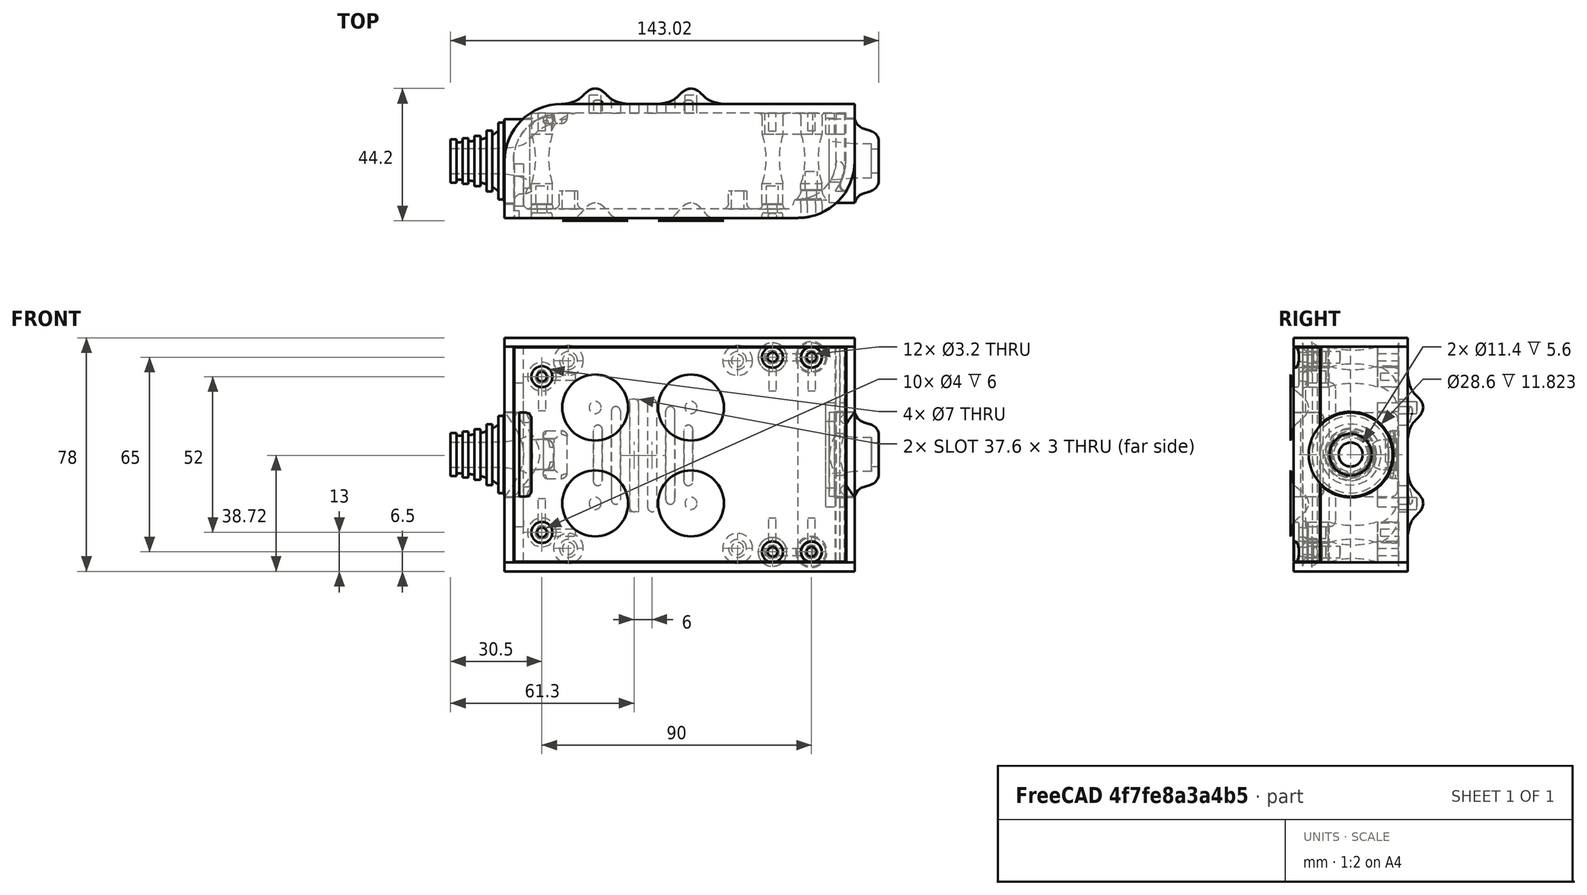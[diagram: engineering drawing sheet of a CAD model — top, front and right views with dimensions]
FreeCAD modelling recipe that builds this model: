
FCSTD DOCUMENT  (FreeCAD 0.19R0.19.2)
Label: enclosure_101
License: All rights reserved
LicenseURL: http://en.wikipedia.org/wiki/All_rights_reserved
objects: Part::Feature×72, Part::Revolution×72, Part::MultiFuse×53, Sketcher::SketchObject×30, Part::Fillet×22, Part::Cylinder×22, Part::Cut×20, Part::Extrusion×19, Part::Box×12, App::MeasureDistance×4
note: 322 computed .brp shape members not serialized (recipe doc carries the construction recipe); baked Part::Feature solids carry a one-line shape summary decoded from their .brp

FEATURE [Sketcher::SketchObject] Sketch  label="topSketch"
  FullyConstrained = true
  sketch-geometry (13):
    g0: LineSegment StartX=117 StartY=19 StartZ=0 EndX=117 EndY=38 EndZ=0
    g1: ArcOfCircle CenterX=98 CenterY=19 CenterZ=0 NormalX=0 NormalY=0 NormalZ=1 AngleXU=0 Radius=19 StartAngle=5.7297 EndAngle=6.28319
    g2: LineSegment StartX=0 StartY=3 StartZ=0 EndX=0 EndY=19 EndZ=0
    g3: LineSegment StartX=19 StartY=38 StartZ=0 EndX=117 EndY=38 EndZ=0
    g4: ArcOfCircle CenterX=19 CenterY=19 CenterZ=0 NormalX=0 NormalY=0 NormalZ=1 AngleXU=0 Radius=19 StartAngle=1.5708 EndAngle=3.14159
    g5: ArcOfCircle CenterX=19 CenterY=19 CenterZ=0 NormalX=0 NormalY=0 NormalZ=1 AngleXU=0 Radius=16 StartAngle=1.5708 EndAngle=3.14159
    g6: ArcOfCircle CenterX=98 CenterY=19 CenterZ=0 NormalX=0 NormalY=0 NormalZ=1 AngleXU=0 Radius=16 StartAngle=5.60905 EndAngle=6.28319
    g7: LineSegment StartX=114 StartY=19 StartZ=0 EndX=114 EndY=35 EndZ=0
    g8: LineSegment StartX=110.5 StartY=9.01251 StartZ=0 EndX=114.163 EndY=9.01251 EndZ=0
    g9: LineSegment StartX=114 StartY=35 StartZ=0 EndX=19 EndY=35 EndZ=0
    g10: LineSegment StartX=0 StartY=3 StartZ=0 EndX=0 EndY=0 EndZ=0
    g11: LineSegment StartX=3 StartY=0 StartZ=0 EndX=0 EndY=0 EndZ=0
    g12: LineSegment StartX=3 StartY=19 StartZ=0 EndX=3 EndY=0 EndZ=0
  constraints (33):
    c: Vertical(g0)
    c: Distance(g0) = 19
    c: Block(g0)
    c: Coincident(g1,g0)
    c: Block(g1)
    c: Vertical(g2)
    c: Block(g2)
    c: Coincident(g3,g0)
    c: Horizontal(g3)
    c: Distance(g3) = 98
    c: Coincident(g4,g3)
    c: Coincident(g4,g2)
    c: Block(g4)
    c: Coincident(g5,g4)
    c: Coincident(g6,g1)
    c: Block(g6)
    c: Block(g5)
    c: Coincident(g7,g6)
    c: Vertical(g7)
    c: Coincident(g8,g6)
    c: Coincident(g8,g1)
    c: Coincident(g9,g7)
    c: Coincident(g9,g5)
    c: Horizontal(g9)
    c: Tangent(g9,g5)
    c: Coincident(g10,g2)
    c: Distance(g10) = 3
    c: Vertical(g10)
    c: Coincident(g11,g10)
    c: Horizontal(g11)
    c: Coincident(g12,g5)
    c: Coincident(g12,g11)
    c: Vertical(g12)
FEATURE [Sketcher::SketchObject] Sketch001  label="bottomSketch"
  FullyConstrained = true
  sketch-geometry (32):
    g0: LineSegment StartX=3.3 StartY=-6.03275e-07 StartZ=0 EndX=98 EndY=-6.03275e-07 EndZ=0
    g1: ArcOfCircle CenterX=98 CenterY=19 CenterZ=0 NormalX=0 NormalY=0 NormalZ=1 AngleXU=0 Radius=19 StartAngle=4.71239 EndAngle=5.71103
    g2: LineSegment StartX=6.3 StartY=8 StartZ=0 EndX=3.3 EndY=8 EndZ=0
    g3: LineSegment StartX=3.3 StartY=8 StartZ=0 EndX=3.3 EndY=-6.03275e-07 EndZ=0
    g4: ArcOfCircle CenterX=8.3 CenterY=5 CenterZ=0 NormalX=0 NormalY=0 NormalZ=1 AngleXU=0 Radius=2 StartAngle=3.14159 EndAngle=4.71239
    g5: LineSegment StartX=6.3 StartY=8 StartZ=0 EndX=6.3 EndY=5 EndZ=0
    g6: ArcOfCircle CenterX=98 CenterY=19 CenterZ=0 NormalX=0 NormalY=0 NormalZ=1 AngleXU=0 Radius=12.7 StartAngle=4.71239 EndAngle=6.28319
    g7: LineSegment StartX=94.7 StartY=3 StartZ=0 EndX=8.3 EndY=3 EndZ=0
    g8-g12: Circle x5 (B-spline internal-alignment scaffolding for g13; pole/knot coordinates omitted)
    g13: BSplineCurve PolesCount=5 KnotsCount=3 Degree=3 IsPeriodic=0
    g14: GeomPoint X=98 Y=6.3 Z=0
    g15: GeomPoint X=96.3938 Y=4.71946 Z=0
    g16: GeomPoint X=94.7 Y=3 Z=0
    g17-g23: Circle x7 (B-spline internal-alignment scaffolding for g24; pole/knot coordinates omitted)
    g24: BSplineCurve PolesCount=7 KnotsCount=5 Degree=3 IsPeriodic=0
    g25-g29: GeomPoint x5 (B-spline internal-alignment scaffolding for g24; pole/knot coordinates omitted)
    g30: ArcOfCircle CenterX=98 CenterY=19 CenterZ=0 NormalX=0 NormalY=0 NormalZ=1 AngleXU=0 Radius=15.7 StartAngle=5.81226 EndAngle=6.28319
    g31: LineSegment StartX=110.7 StartY=19 StartZ=0 EndX=113.7 EndY=19 EndZ=0
  constraints (41):
    c: Horizontal(g0)
    c: Coincident(g1,g0)
    c: Block(g1)
    c: Horizontal(g2)
    c: Distance(g2) = 3
    c: Coincident(g3,g2)
    c: Vertical(g3)
    c: Coincident(g3,g0)
    c: Block(g4)
    c: Block(g2)
    c: Coincident(g5,g2)
    c: Coincident(g5,g4)
    c: Vertical(g5)
    c: Coincident(g6,g1)
    c: Block(g6)
    c: Coincident(g7,g4)
    c: Horizontal(g7)
    c: Block(g0)
    c: Block(g7)
    c: Block(g3)
    c: Coincident(g13,g6)
    c: Weight(g8) = 1
    c: Equal(g8, g9-g12) x4
    c: Coincident(g13,g7)
    c: InternalAlignment(g8-g12 -> g13) x5
    c: InternalAlignment(g14,g13)
    c: InternalAlignment(g15,g13)
    c: InternalAlignment(g16,g13)
    c: Block(g13)
    c: Weight(g17) = 1
    c: Equal(g17, g18-g23) x6
    c: Coincident(g24,g1)
    c: InternalAlignment(g17-g23 -> g24) x7
    c: InternalAlignment(g25-g29 -> g24) x5
    c: Block(g24)
    c: Coincident(g30,g24)
    c: Coincident(g31,g6)
    c: Coincident(g31,g30)
    c: Horizontal(g31)
    c: Block(g31)
    c: Block(g30)
FEATURE [Part::Extrusion] Extrude  label="top"
  Base = -> Sketch
  Dir = (0,0,1)
  DirMode = 2
  FaceMakerClass = Part::FaceMakerBullseye
  LengthFwd = 72
  LengthRev = 0
  Solid = true
  Symmetric = false
FEATURE [Part::Extrusion] Extrude001  label="bottom"
  Base = -> Sketch001
  Dir = (0,0,1)
  DirMode = 2
  FaceMakerClass = Part::FaceMakerBullseye
  LengthFwd = 71.4
  LengthRev = 0
  Placement = pos=(0,0,0.3) rot=(0,0,1;0rad)
  Solid = true
  Symmetric = false
FEATURE [Sketcher::SketchObject] Sketch002  label="topSketch001"
  FullyConstrained = true
  sketch-geometry (6):
    g0: LineSegment StartX=19 StartY=38 StartZ=0 EndX=117 EndY=38 EndZ=0
    g1: ArcOfCircle CenterX=19 CenterY=19 CenterZ=0 NormalX=0 NormalY=0 NormalZ=1 AngleXU=0 Radius=19 StartAngle=1.5708 EndAngle=3.14159
    g2: LineSegment StartX=117 StartY=38 StartZ=0 EndX=117 EndY=19 EndZ=0
    g3: LineSegment StartX=98 StartY=1.0161e-12 StartZ=0 EndX=5.22862e-06 EndY=1.0161e-12 EndZ=0
    g4: LineSegment StartX=5.22862e-06 StartY=19 StartZ=0 EndX=5.22862e-06 EndY=1.0161e-12 EndZ=0
    g5: ArcOfCircle CenterX=98 CenterY=19 CenterZ=0 NormalX=0 NormalY=0 NormalZ=1 AngleXU=0 Radius=19 StartAngle=4.71239 EndAngle=6.28319
  constraints (16):
    c: Horizontal(g0)
    c: Distance(g0) = 98
    c: Coincident(g1,g0)
    c: Block(g1)
    c: Coincident(g2,g0)
    c: Vertical(g2)
    c: Distance(g2) = 19
    c: Horizontal(g3)
    c: Coincident(g4,g1)
    c: Vertical(g4)
    c: Coincident(g3,g4)
    c: Block(g3)
    c: Coincident(g5,g2)
    c: Coincident(g5,g3)
    c: Block(g0)
    c: Block(g5)
FEATURE [Part::Extrusion] Extrude002  label="sideA"
  Base = -> Sketch002
  Dir = (0,0,1)
  DirMode = 2
  FaceMakerClass = Part::FaceMakerBullseye
  LengthFwd = 3
  LengthRev = 0
  Placement = pos=(0,0,-3) rot=(0,0,1;0rad)
  Solid = true
  Symmetric = false
FEATURE [Sketcher::SketchObject] Sketch003  label="topSketch002"
  FullyConstrained = true
  sketch-geometry (6):
    g0: LineSegment StartX=19 StartY=38 StartZ=0 EndX=117 EndY=38 EndZ=0
    g1: ArcOfCircle CenterX=19 CenterY=19 CenterZ=0 NormalX=0 NormalY=0 NormalZ=1 AngleXU=0 Radius=19 StartAngle=1.5708 EndAngle=3.14159
    g2: LineSegment StartX=117 StartY=38 StartZ=0 EndX=117 EndY=19 EndZ=0
    g3: LineSegment StartX=98 StartY=1.0161e-12 StartZ=0 EndX=5.22862e-06 EndY=1.0161e-12 EndZ=0
    g4: LineSegment StartX=5.22862e-06 StartY=19 StartZ=0 EndX=5.22862e-06 EndY=1.0161e-12 EndZ=0
    g5: ArcOfCircle CenterX=98 CenterY=19 CenterZ=0 NormalX=0 NormalY=0 NormalZ=1 AngleXU=0 Radius=19 StartAngle=4.71239 EndAngle=6.28319
  constraints (16):
    c: Horizontal(g0)
    c: Distance(g0) = 98
    c: Coincident(g1,g0)
    c: Block(g1)
    c: Coincident(g2,g0)
    c: Vertical(g2)
    c: Distance(g2) = 19
    c: Horizontal(g3)
    c: Coincident(g4,g1)
    c: Vertical(g4)
    c: Coincident(g3,g4)
    c: Block(g3)
    c: Coincident(g5,g2)
    c: Coincident(g5,g3)
    c: Block(g0)
    c: Block(g5)
FEATURE [Part::Extrusion] Extrude003  label="sideB"
  Base = -> Sketch003
  Dir = (0,0,1)
  DirMode = 2
  FaceMakerClass = Part::FaceMakerBullseye
  LengthFwd = 3
  LengthRev = 0
  Placement = pos=(0,0,72) rot=(0,0,1;0rad)
  Solid = true
  Symmetric = false
FEATURE [Sketcher::SketchObject] Sketch004
  FullyConstrained = true
  MapMode = 3
  Placement = pos=(0,0,0) rot=(1,0,0;1.5708rad)
  Support = -> [Extrude]
  sketch-geometry (8):
    g0: Circle CenterX=80.351 CenterY=-67.6202 CenterZ=0 NormalX=0 NormalY=0 NormalZ=1 AngleXU=0 Radius=2
    g1: Circle CenterX=80.351 CenterY=-67.6202 CenterZ=0 NormalX=0 NormalY=0 NormalZ=1 AngleXU=0 Radius=3
    g2: Circle CenterX=80.351 CenterY=-4.92017 CenterZ=0 NormalX=0 NormalY=0 NormalZ=1 AngleXU=0 Radius=2
    g3: Circle CenterX=80.351 CenterY=-4.92017 CenterZ=0 NormalX=0 NormalY=0 NormalZ=1 AngleXU=0 Radius=3
    g4: Circle CenterX=23.851 CenterY=-4.92017 CenterZ=0 NormalX=0 NormalY=0 NormalZ=1 AngleXU=0 Radius=2
    g5: Circle CenterX=23.851 CenterY=-4.92017 CenterZ=0 NormalX=0 NormalY=0 NormalZ=1 AngleXU=0 Radius=3
    g6: Circle CenterX=23.851 CenterY=-67.6202 CenterZ=0 NormalX=0 NormalY=0 NormalZ=1 AngleXU=0 Radius=2
    g7: Circle CenterX=23.851 CenterY=-67.6202 CenterZ=0 NormalX=0 NormalY=0 NormalZ=1 AngleXU=0 Radius=3
  constraints (8):
    c: Block(g3)
    c: Block(g2)
    c: Block(g1)
    c: Block(g0)
    c: Block(g6)
    c: Block(g7)
    c: Block(g4)
    c: Block(g5)
FEATURE [Part::Extrusion] Extrude004
  Base = -> Sketch004
  Dir = (0,-1,2e-16)
  DirMode = 2
  FaceMakerClass = Part::FaceMakerBullseye
  LengthFwd = 6
  LengthRev = 0
  Placement = pos=(0,9,0) rot=(0,0,1;0rad)
  Solid = true
  Symmetric = false
FEATURE [Sketcher::SketchObject] Sketch005
  FullyConstrained = true
  MapMode = 3
  Placement = pos=(0,0,0) rot=(1,0,0;1.5708rad)
  Support = -> [Extrude]
  sketch-geometry (8):
    g0: Circle CenterX=80.351 CenterY=-67.6202 CenterZ=0 NormalX=0 NormalY=0 NormalZ=1 AngleXU=0 Radius=3
    g1: Circle CenterX=80.351 CenterY=-4.92017 CenterZ=0 NormalX=0 NormalY=0 NormalZ=1 AngleXU=0 Radius=3
    g2: Circle CenterX=23.851 CenterY=-4.92017 CenterZ=0 NormalX=0 NormalY=0 NormalZ=1 AngleXU=0 Radius=3
    g3: Circle CenterX=23.851 CenterY=-67.6202 CenterZ=0 NormalX=0 NormalY=0 NormalZ=1 AngleXU=0 Radius=3
    g4: Circle CenterX=23.851 CenterY=-67.6202 CenterZ=0 NormalX=0 NormalY=0 NormalZ=1 AngleXU=0 Radius=5
    g5: Circle CenterX=80.351 CenterY=-67.6202 CenterZ=0 NormalX=0 NormalY=0 NormalZ=1 AngleXU=0 Radius=5
    g6: Circle CenterX=23.851 CenterY=-4.92017 CenterZ=0 NormalX=0 NormalY=0 NormalZ=1 AngleXU=0 Radius=5
    g7: Circle CenterX=80.351 CenterY=-4.92017 CenterZ=0 NormalX=0 NormalY=0 NormalZ=1 AngleXU=0 Radius=5
  constraints (8):
    c: Block(g1)
    c: Block(g0)
    c: Block(g3)
    c: Block(g2)
    c: Block(g5)
    c: Block(g4)
    c: Block(g6)
    c: Block(g7)
FEATURE [Part::Extrusion] Extrude005
  Base = -> Sketch005
  Dir = (0,-1,2e-16)
  DirMode = 2
  FaceMakerClass = Part::FaceMakerBullseye
  LengthFwd = 2
  LengthRev = 0
  Solid = true
  Symmetric = false
FEATURE [Sketcher::SketchObject] Sketch006
  FullyConstrained = true
  MapMode = 3
  Placement = pos=(0,0,0) rot=(1,0,0;1.5708rad)
  sketch-geometry (8):
    g0: Circle CenterX=80.351 CenterY=-67.6202 CenterZ=0 NormalX=0 NormalY=0 NormalZ=1 AngleXU=0 Radius=3
    g1: Circle CenterX=80.351 CenterY=-4.92017 CenterZ=0 NormalX=0 NormalY=0 NormalZ=1 AngleXU=0 Radius=3
    g2: Circle CenterX=23.851 CenterY=-4.92017 CenterZ=0 NormalX=0 NormalY=0 NormalZ=1 AngleXU=0 Radius=3
    g3: Circle CenterX=23.851 CenterY=-67.6202 CenterZ=0 NormalX=0 NormalY=0 NormalZ=1 AngleXU=0 Radius=3
    g4: Circle CenterX=23.851 CenterY=-67.6202 CenterZ=0 NormalX=0 NormalY=0 NormalZ=1 AngleXU=0 Radius=5
    g5: Circle CenterX=80.351 CenterY=-67.6202 CenterZ=0 NormalX=0 NormalY=0 NormalZ=1 AngleXU=0 Radius=5
    g6: Circle CenterX=23.851 CenterY=-4.92017 CenterZ=0 NormalX=0 NormalY=0 NormalZ=1 AngleXU=0 Radius=5
    g7: Circle CenterX=80.351 CenterY=-4.92017 CenterZ=0 NormalX=0 NormalY=0 NormalZ=1 AngleXU=0 Radius=5
  constraints (8):
    c: Block(g1)
    c: Block(g0)
    c: Block(g3)
    c: Block(g2)
    c: Block(g5)
    c: Block(g4)
    c: Block(g6)
    c: Block(g7)
FEATURE [Part::Extrusion] Extrude007
  Base = -> Sketch006
  Dir = (0,-1,2e-16)
  DirMode = 2
  FaceMakerClass = Part::FaceMakerBullseye
  LengthFwd = 2
  LengthRev = 0
  Solid = true
  Symmetric = false
FEATURE [Part::Fillet] Fillet
  Base = -> Extrude007
  Edges = 4 edges r=1.99: [Edge6,Edge12,Edge18,Edge24]
FEATURE [Part::Cut] Cut
  Base = -> Extrude005
  Placement = pos=(0,5,0) rot=(0,0,1;0rad)
  Tool = -> Fillet
FEATURE [Part::MultiFuse] Fusion  label="pCBScrews"
  Placement = pos=(-2.5,0,72.3) rot=(0,0,1;0rad)
  Shapes = -> [Extrude004,Cut]
FEATURE [App::MeasureDistance] Distance  label="Distance: 0.69 mm"
  Distance = 0.685967
  P1 = (24.0138,2.9647,0.3)
  P2 = (23.8901,3,-0.373787)
FEATURE [App::MeasureDistance] Distance001  label="Distance: 0.53 mm"
  Distance = 0.533607
  P1 = (80.2939,3,72.2334)
  P2 = (80.281,2.99661,71.7)
FEATURE [Part::Fillet] Fillet001
  Base = -> Extrude001
  Edges = 1 edges r=2.4: [Edge17]
FEATURE [Part::Fillet] Fillet002  label="bottom001"
  Base = -> Fillet001
  Edges = 1 edges r=2.4: [Edge36]
FEATURE [Part::Fillet] Fillet003  label="top001"
  Base = -> Extrude
  Edges = 1 edges r=2: [Edge1]
FEATURE [Sketcher::SketchObject] Sketch007
  FullyConstrained = true
  sketch-geometry (16):
    g0: LineSegment StartX=4 StartY=0 StartZ=0 EndX=4 EndY=2.4 EndZ=0
    g1: LineSegment StartX=4 StartY=2.4 StartZ=0 EndX=7 EndY=2.4 EndZ=0
    g2: LineSegment StartX=4 StartY=0 StartZ=0 EndX=5.7 EndY=0 EndZ=0
    g3: LineSegment StartX=5.7 StartY=0 StartZ=0 EndX=5.7 EndY=-5.6 EndZ=0
    g4-g8: Circle x5 (B-spline internal-alignment scaffolding for g9; pole/knot coordinates omitted)
    g9: BSplineCurve PolesCount=5 KnotsCount=3 Degree=3 IsPeriodic=0
    g10: GeomPoint X=7 Y=2.4 Z=0
    g11: GeomPoint X=10.4582 Y=-1.55472 Z=0
    g12: GeomPoint X=14 Y=-5.6 Z=0
    g13: LineSegment StartX=14 StartY=-5.6 StartZ=0 EndX=14 EndY=-14.1 EndZ=0
    g14: LineSegment StartX=14 StartY=-14.1 StartZ=0 EndX=6.5 EndY=-14.1 EndZ=0
    g15: LineSegment StartX=5.7 StartY=-5.6 StartZ=0 EndX=6.5 EndY=-14.1 EndZ=0
  constraints (28):
    c: Distance(g0) = 2.4
    c: Vertical(g0)
    c: Block(g0)
    c: Coincident(g1,g0)
    c: Horizontal(g1)
    c: Distance(g1) = 3
    c: Coincident(g2,g0)
    c: Horizontal(g2)
    c: Distance(g2) = 1.7
    c: Coincident(g3,g2)
    c: Vertical(g3)
    c: Distance(g3) = 5.6
    c: Coincident(g9,g1)
    c: Weight(g4) = 1
    c: Equal(g4, g5-g8) x4
    c: InternalAlignment(g4-g8 -> g9) x5
    c: InternalAlignment(g10,g9)
    c: InternalAlignment(g11,g9)
    c: InternalAlignment(g12,g9)
    c: Block(g9)
    c: Coincident(g13,g9)
    c: Vertical(g13)
    c: Distance(g13) = 8.5
    c: Coincident(g14,g13)
    c: Horizontal(g14)
    c: Distance(g14) = 7.5
    c: Coincident(g15,g3)
    c: Coincident(g15,g14)
FEATURE [Part::Feature] Face
  shape: bbox 10 x 16.5 x 2e-07 mm, 1 faces, 0 solids (baked)
FEATURE [Part::Revolution] Revolve  label="plugHousing"
  Angle = 360
  Axis = (0,1,0)
  Base = (0,0,0)
  FaceMakerClass = Part::FaceMakerBullseye
  Placement = pos=(0,0,36.15) rot=(0,0,1;0rad)
  Solid = false
  Source = -> Face
  Symmetric = false
FEATURE [Part::Feature] Face001
  shape: bbox 10 x 16.5 x 2e-07 mm, 1 faces, 0 solids (baked)
FEATURE [Part::Revolution] Revolve001  label="plugHousing001"
  Angle = 360
  Axis = (0,1,0)
  Base = (0,0,0)
  FaceMakerClass = Part::FaceMakerBullseye
  Placement = pos=(0,0,36.15) rot=(0,0,1;0rad)
  Solid = false
  Source = -> Face001
  Symmetric = false
FEATURE [Part::MultiFuse] Fusion001  label="plugHousing002"
  Placement = pos=(0,0,0) rot=(0,0,1;1.5708rad)
  Shapes = -> [Revolve001,Revolve]
FEATURE [Part::Feature] Face002
  shape: bbox 10 x 16.5 x 2e-07 mm, 1 faces, 0 solids (baked)
FEATURE [Part::Revolution] Revolve003  label="plugHousing005"
  Angle = 360
  Axis = (0,1,0)
  Base = (0,0,0)
  FaceMakerClass = Part::FaceMakerBullseye
  Placement = pos=(0,0,36.15) rot=(0,0,1;0rad)
  Solid = false
  Source = -> Face002
  Symmetric = false
FEATURE [Part::Feature] Face003
  shape: bbox 10 x 16.5 x 2e-07 mm, 1 faces, 0 solids (baked)
FEATURE [Part::Revolution] Revolve002  label="plugHousing003"
  Angle = 360
  Axis = (0,1,0)
  Base = (0,0,0)
  FaceMakerClass = Part::FaceMakerBullseye
  Placement = pos=(0,0,36.15) rot=(0,0,1;0rad)
  Solid = false
  Source = -> Face003
  Symmetric = false
FEATURE [Part::MultiFuse] Fusion002  label="plugHousing004"
  Placement = pos=(0,0,0) rot=(0,0,1;1.5708rad)
  Shapes = -> [Revolve002,Revolve003]
FEATURE [Part::MultiFuse] Fusion003  label="plugHousing006"
  Placement = pos=(0,19,0) rot=(0,0,1;3.14159rad)
  Shapes = -> [Fusion002,Fusion001]
FEATURE [Part::Feature] Face004
  shape: bbox 10 x 16.5 x 2e-07 mm, 1 faces, 0 solids (baked)
FEATURE [Part::Revolution] Revolve006  label="plugHousing010"
  Angle = 360
  Axis = (0,1,0)
  Base = (0,0,0)
  FaceMakerClass = Part::FaceMakerBullseye
  Placement = pos=(0,0,36.15) rot=(0,0,1;0rad)
  Solid = false
  Source = -> Face004
  Symmetric = false
FEATURE [Part::Feature] Face005
  shape: bbox 10 x 16.5 x 2e-07 mm, 1 faces, 0 solids (baked)
FEATURE [Part::Revolution] Revolve007  label="plugHousing011"
  Angle = 360
  Axis = (0,1,0)
  Base = (0,0,0)
  FaceMakerClass = Part::FaceMakerBullseye
  Placement = pos=(0,0,36.15) rot=(0,0,1;0rad)
  Solid = false
  Source = -> Face005
  Symmetric = false
FEATURE [Part::Feature] Face006
  shape: bbox 10 x 16.5 x 2e-07 mm, 1 faces, 0 solids (baked)
FEATURE [Part::Revolution] Revolve004  label="plugHousing007"
  Angle = 360
  Axis = (0,1,0)
  Base = (0,0,0)
  FaceMakerClass = Part::FaceMakerBullseye
  Placement = pos=(0,0,36.15) rot=(0,0,1;0rad)
  Solid = false
  Source = -> Face006
  Symmetric = false
FEATURE [Part::MultiFuse] Fusion004  label="plugHousing009"
  Placement = pos=(0,0,0) rot=(0,0,1;1.5708rad)
  Shapes = -> [Revolve004,Revolve007]
FEATURE [Part::Feature] Face007
  shape: bbox 10 x 16.5 x 2e-07 mm, 1 faces, 0 solids (baked)
FEATURE [Part::Revolution] Revolve005  label="plugHousing008"
  Angle = 360
  Axis = (0,1,0)
  Base = (0,0,0)
  FaceMakerClass = Part::FaceMakerBullseye
  Placement = pos=(0,0,36.15) rot=(0,0,1;0rad)
  Solid = false
  Source = -> Face007
  Symmetric = false
FEATURE [Part::MultiFuse] Fusion005  label="plugHousing012"
  Placement = pos=(0,0,0) rot=(0,0,1;1.5708rad)
  Shapes = -> [Revolve006,Revolve005]
FEATURE [Part::MultiFuse] Fusion006  label="plugHousing013"
  Placement = pos=(0,19,0) rot=(0,0,1;3.14159rad)
  Shapes = -> [Fusion005,Fusion004]
FEATURE [Part::MultiFuse] Fusion007  label="plugHousing014"
  Placement = pos=(122.621,0,-0.15) rot=(0,0,1;0rad)
  Shapes = -> [Fusion003,Fusion006]
FEATURE [Part::Cylinder] Cylinder002
  Angle = 360
  AttacherType = Attacher::AttachEngine3D
  Height = 20
  Placement = pos=(0,0,36.15) rot=(0,0,1;0rad)
  Radius = 4
FEATURE [Part::Cylinder] Cylinder003
  Angle = 360
  AttacherType = Attacher::AttachEngine3D
  Height = 10
  Placement = pos=(0,0,36.15) rot=(0,0,1;0rad)
  Radius = 4
FEATURE [Part::MultiFuse] Fusion009  label="removeToCreateHoleForPlugHousing"
  Placement = pos=(70,19,36.15) rot=(0,1,0;1.5708rad)
  Shapes = -> [Cylinder002,Cylinder003]
FEATURE [Part::Cylinder] Cylinder004
  Angle = 360
  AttacherType = Attacher::AttachEngine3D
  Height = 20
  Placement = pos=(0,0,36.15) rot=(0,0,1;0rad)
  Radius = 4
FEATURE [Part::Cylinder] Cylinder005
  Angle = 360
  AttacherType = Attacher::AttachEngine3D
  Height = 10
  Placement = pos=(0,0,36.15) rot=(0,0,1;0rad)
  Radius = 4
FEATURE [Part::MultiFuse] Fusion010  label="removeToCreateHoleForPlugHousing001"
  Placement = pos=(70,19,36.15) rot=(0,1,0;1.5708rad)
  Shapes = -> [Cylinder004,Cylinder005]
FEATURE [Part::Cut] Cut001
  Base = -> Fillet003
  Tool = -> Fusion010
FEATURE [Part::Cut] Cut002  label="Bottom"
  Base = -> Fillet002
  Tool = -> Fusion009
FEATURE [Part::Feature] Face008
  shape: bbox 10 x 16.5 x 2e-07 mm, 1 faces, 0 solids (baked)
FEATURE [Part::Revolution] Revolve011  label="plugHousing021"
  Angle = 360
  Axis = (0,1,0)
  Base = (0,0,0)
  FaceMakerClass = Part::FaceMakerBullseye
  Placement = pos=(0,0,36.15) rot=(0,0,1;0rad)
  Solid = false
  Source = -> Face008
  Symmetric = false
FEATURE [Part::Feature] Face009
  shape: bbox 10 x 16.5 x 2e-07 mm, 1 faces, 0 solids (baked)
FEATURE [Part::Revolution] Revolve012  label="plugHousing022"
  Angle = 360
  Axis = (0,1,0)
  Base = (0,0,0)
  FaceMakerClass = Part::FaceMakerBullseye
  Placement = pos=(0,0,36.15) rot=(0,0,1;0rad)
  Solid = false
  Source = -> Face009
  Symmetric = false
FEATURE [Part::Feature] Face010 .. Face013  x4 (patterned run collapsed; names and placements below)
  shape: bbox 10 x 16.5 x 2e-07 mm, 1 faces, 0 solids (baked)
FEATURE [Part::Revolution] Revolve015  label="plugHousing027"
  Angle = 360
  Axis = (0,1,0)
  Base = (0,0,0)
  FaceMakerClass = Part::FaceMakerBullseye
  Placement = pos=(0,0,36.15) rot=(0,0,1;0rad)
  Solid = false
  Source = -> Face013
  Symmetric = false
FEATURE [Part::Feature] Face014
  shape: bbox 10 x 16.5 x 2e-07 mm, 1 faces, 0 solids (baked)
FEATURE [Part::Feature] Face015
  shape: bbox 10 x 16.5 x 2e-07 mm, 1 faces, 0 solids (baked)
FEATURE [Part::Feature] Face016
  shape: bbox 10 x 16.5 x 2e-07 mm, 1 faces, 0 solids (baked)
FEATURE [Part::Revolution] Revolve019  label="plugHousing033"
  Angle = 360
  Axis = (0,1,0)
  Base = (0,0,0)
  FaceMakerClass = Part::FaceMakerBullseye
  Placement = pos=(0,0,36.15) rot=(0,0,1;0rad)
  Solid = false
  Source = -> Face016
  Symmetric = false
FEATURE [Part::Feature] Face017
  shape: bbox 10 x 16.5 x 2e-07 mm, 1 faces, 0 solids (baked)
FEATURE [Part::Revolution] Revolve020  label="plugHousing034"
  Angle = 360
  Axis = (0,1,0)
  Base = (0,0,0)
  FaceMakerClass = Part::FaceMakerBullseye
  Placement = pos=(0,0,36.15) rot=(0,0,1;0rad)
  Solid = false
  Source = -> Face017
  Symmetric = false
FEATURE [Part::Feature] Face018
  shape: bbox 10 x 16.5 x 2e-07 mm, 1 faces, 0 solids (baked)
FEATURE [Part::Revolution] Revolve016  label="plugHousing030"
  Angle = 360
  Axis = (0,1,0)
  Base = (0,0,0)
  FaceMakerClass = Part::FaceMakerBullseye
  Placement = pos=(0,0,36.15) rot=(0,0,1;0rad)
  Solid = false
  Source = -> Face018
  Symmetric = false
FEATURE [Part::MultiFuse] Fusion020  label="plugHousing038"
  Placement = pos=(0,0,0) rot=(0,0,1;1.5708rad)
  Shapes = -> [Revolve016,Revolve020]
FEATURE [Part::Feature] Face019
  shape: bbox 10 x 16.5 x 2e-07 mm, 1 faces, 0 solids (baked)
FEATURE [Part::Feature] Face020
  shape: bbox 10 x 16.5 x 2e-07 mm, 1 faces, 0 solids (baked)
FEATURE [Part::Revolution] Revolve017  label="plugHousing031"
  Angle = 360
  Axis = (0,1,0)
  Base = (0,0,0)
  FaceMakerClass = Part::FaceMakerBullseye
  Placement = pos=(0,0,36.15) rot=(0,0,1;0rad)
  Solid = false
  Source = -> Face020
  Symmetric = false
FEATURE [Part::MultiFuse] Fusion021  label="plugHousing039"
  Placement = pos=(0,0,0) rot=(0,0,1;1.5708rad)
  Shapes = -> [Revolve019,Revolve017]
FEATURE [Part::MultiFuse] Fusion023  label="plugHousing041"
  Placement = pos=(0,19,0) rot=(0,0,1;3.14159rad)
  Shapes = -> [Fusion021,Fusion020]
FEATURE [Part::Revolution] Revolve022  label="plugHousing043"
  Angle = 360
  Axis = (0,1,0)
  Base = (0,0,0)
  FaceMakerClass = Part::FaceMakerBullseye
  Placement = pos=(0,0,36.15) rot=(0,0,1;0rad)
  Solid = false
  Source = -> Face019
  Symmetric = false
FEATURE [Part::Feature] Face021
  shape: bbox 10 x 16.5 x 2e-07 mm, 1 faces, 0 solids (baked)
FEATURE [Part::Revolution] Revolve023  label="plugHousing044"
  Angle = 360
  Axis = (0,1,0)
  Base = (0,0,0)
  FaceMakerClass = Part::FaceMakerBullseye
  Placement = pos=(0,0,36.15) rot=(0,0,1;0rad)
  Solid = false
  Source = -> Face021
  Symmetric = false
FEATURE [Part::Feature] Face022
  shape: bbox 10 x 16.5 x 2e-07 mm, 1 faces, 0 solids (baked)
FEATURE [Part::Revolution] Revolve018  label="plugHousing032"
  Angle = 360
  Axis = (0,1,0)
  Base = (0,0,0)
  FaceMakerClass = Part::FaceMakerBullseye
  Placement = pos=(0,0,36.15) rot=(0,0,1;0rad)
  Solid = false
  Source = -> Face022
  Symmetric = false
FEATURE [Part::MultiFuse] Fusion022  label="plugHousing040"
  Placement = pos=(0,0,0) rot=(0,0,1;1.5708rad)
  Shapes = -> [Revolve018,Revolve023]
FEATURE [Part::Feature] Face023
  shape: bbox 10 x 16.5 x 2e-07 mm, 1 faces, 0 solids (baked)
FEATURE [Part::Revolution] Revolve021  label="plugHousing035"
  Angle = 360
  Axis = (0,1,0)
  Base = (0,0,0)
  FaceMakerClass = Part::FaceMakerBullseye
  Placement = pos=(0,0,36.15) rot=(0,0,1;0rad)
  Solid = false
  Source = -> Face023
  Symmetric = false
FEATURE [Part::MultiFuse] Fusion018  label="plugHousing036"
  Placement = pos=(0,0,0) rot=(0,0,1;1.5708rad)
  Shapes = -> [Revolve022,Revolve021]
FEATURE [Part::MultiFuse] Fusion019  label="plugHousing037"
  Placement = pos=(0,19,0) rot=(0,0,1;3.14159rad)
  Shapes = -> [Fusion018,Fusion022]
FEATURE [Part::MultiFuse] Fusion024  label="plugHousing042"
  Placement = pos=(122.621,0,-0.15) rot=(0,0,1;0rad)
  Shapes = -> [Fusion023,Fusion019]
FEATURE [Part::Cylinder] Cylinder006
  Angle = 360
  AttacherType = Attacher::AttachEngine3D
  Height = 20
  Placement = pos=(0,0,36.15) rot=(0,0,1;0rad)
  Radius = 14.3
FEATURE [Part::Cylinder] Cylinder007
  Angle = 360
  AttacherType = Attacher::AttachEngine3D
  Height = 10
  Placement = pos=(0,0,36.15) rot=(0,0,1;0rad)
  Radius = 4
FEATURE [Part::MultiFuse] Fusion026  label="removeToCreteHoleForPlugHousing"
  Placement = pos=(70,19,36) rot=(0,1,0;1.5708rad)
  Shapes = -> [Cylinder006,Cylinder007]
FEATURE [Part::Box] Box001  label="Cube001"
  AttacherType = Attacher::AttachEngine3D
  Height = 28
  Length = 3
  Placement = pos=(110.7,19,22) rot=(0,0,1;0rad)
  Width = 15.7
FEATURE [Part::Cut] Cut003  label="top002"
  Base = -> Cut001
  Tool = -> Fusion007
FEATURE [Part::Revolution] Revolve008  label="plugHousing015"
  Angle = 360
  Axis = (0,1,0)
  Base = (0,0,0)
  FaceMakerClass = Part::FaceMakerBullseye
  Placement = pos=(0,0,36.15) rot=(0,0,1;0rad)
  Solid = false
  Source = -> Face010
  Symmetric = false
FEATURE [Part::MultiFuse] Fusion013  label="plugHousing020"
  Placement = pos=(0,0,0) rot=(0,0,1;1.5708rad)
  Shapes = -> [Revolve008,Revolve012]
FEATURE [Part::Cut] Cut004  label="top003"
  Base = -> Cut003
  Placement = pos=(1,0,0) rot=(0,0,1;0rad)
  Tool = -> Fusion026
FEATURE [Part::Cylinder] Cylinder008
  Angle = 360
  AttacherType = Attacher::AttachEngine3D
  Height = 20
  Placement = pos=(0,0,36.15) rot=(0,0,1;0rad)
  Radius = 10.3
FEATURE [Part::Cylinder] Cylinder009
  Angle = 360
  AttacherType = Attacher::AttachEngine3D
  Height = 10
  Placement = pos=(0,0,36.15) rot=(0,0,1;0rad)
  Radius = 4
FEATURE [Part::MultiFuse] Fusion027  label="removeToCreteHoleForPlugHousing001"
  Placement = pos=(70,19,36) rot=(0,1,0;1.5708rad)
  Shapes = -> [Cylinder008,Cylinder009]
FEATURE [Part::Cut] Cut005  label="plugHousingTab"
  Base = -> Box001
  Tool = -> Fusion027
FEATURE [Part::MultiFuse] Fusion028  label="plugHousing045"
  Shapes = -> [Fusion024,Cut005]
FEATURE [Part::Box] Box002  label="Cube002"
  AttacherType = Attacher::AttachEngine3D
  Height = 28.8
  Length = 3
  Placement = pos=(107.3,28,21.6) rot=(0,0,1;0rad)
  Width = 7
FEATURE [Part::Box] Box003  label="Cube003"
  AttacherType = Attacher::AttachEngine3D
  Height = 3
  Length = 6.4
  Placement = pos=(107.3,28,18.6) rot=(0,0,1;0rad)
  Width = 7
FEATURE [Part::Box] Box004  label="Cube004"
  AttacherType = Attacher::AttachEngine3D
  Height = 3
  Length = 6.4
  Placement = pos=(107.3,28,50.4) rot=(0,0,1;0rad)
  Width = 7
FEATURE [Part::MultiFuse] Fusion029  label="plugHousingBracketHolder"
  Shapes = -> [Box004,Box002,Box003]
FEATURE [Part::Cylinder] Cylinder010
  Angle = 360
  AttacherType = Attacher::AttachEngine3D
  Height = 20
  Placement = pos=(0,0,36.15) rot=(0,0,1;0rad)
  Radius = 14.3
FEATURE [Part::Cylinder] Cylinder011
  Angle = 360
  AttacherType = Attacher::AttachEngine3D
  Height = 10
  Placement = pos=(0,0,36.15) rot=(0,0,1;0rad)
  Radius = 4
FEATURE [Part::MultiFuse] Fusion030  label="removeToCreteHoleForPlugHousing002"
  Placement = pos=(70,19,36) rot=(0,1,0;1.5708rad)
  Shapes = -> [Cylinder010,Cylinder011]
FEATURE [Part::Cut] Cut006  label="plugHousingBracketHolder001"
  Base = -> Fusion029
  Tool = -> Fusion030
FEATURE [Part::Cylinder] Cylinder012
  Angle = 360
  AttacherType = Attacher::AttachEngine3D
  Height = 20
  Placement = pos=(0,0,36.15) rot=(0,0,1;0rad)
  Radius = 7
FEATURE [Part::Cylinder] Cylinder013
  Angle = 360
  AttacherType = Attacher::AttachEngine3D
  Height = 10
  Placement = pos=(0,0,36.15) rot=(0,0,1;0rad)
  Radius = 4
FEATURE [Part::MultiFuse] Fusion032  label="removeToCreteHoleForPlugHousing003"
  Placement = pos=(70,19,36) rot=(0,1,0;1.5708rad)
  Shapes = -> [Cylinder012,Cylinder013]
FEATURE [Part::Cut] Cut007  label="bottom002"
  Base = -> Cut002
  Tool = -> Fusion032
FEATURE [Sketcher::SketchObject] Sketch008
  FullyConstrained = true
  sketch-geometry (54):
    g0: LineSegment StartX=-4.2 StartY=0 StartZ=0 EndX=-6.2 EndY=0 EndZ=0
    g1: LineSegment StartX=-14 StartY=-18 StartZ=0 EndX=-14 EndY=-26.5 EndZ=0
    g2: LineSegment StartX=-4.2 StartY=0 StartZ=0 EndX=-4.2 EndY=-13.4877 EndZ=0
    g3: Circle CenterX=-4.2 CenterY=-13.4877 CenterZ=0 NormalX=0 NormalY=0 NormalZ=1 AngleXU=0 Radius=1
    g4: Circle CenterX=-4.2 CenterY=-26.5 CenterZ=0 NormalX=0 NormalY=0 NormalZ=1 AngleXU=0 Radius=1
    g5: Circle CenterX=-8.2 CenterY=-26.5 CenterZ=0 NormalX=0 NormalY=0 NormalZ=1 AngleXU=0 Radius=1
    g6: BSplineCurve PolesCount=3 KnotsCount=2 Degree=2 IsPeriodic=0
    g7: GeomPoint X=-4.2 Y=-13.4877 Z=0
    g8: GeomPoint X=-8.2 Y=-26.5 Z=0
    g9: LineSegment StartX=-14 StartY=-26.5 StartZ=0 EndX=-8.2 EndY=-26.5 EndZ=0
    g10: LineSegment StartX=-10.15 StartY=-12 StartZ=0 EndX=-10.15 EndY=-14 EndZ=0
    g11: LineSegment StartX=-12.8401 StartY=-16 StartZ=0 EndX=-10.1571 EndY=-16 EndZ=0
    g12: LineSegment StartX=-10.15 StartY=-14 StartZ=0 EndX=-8.70761 EndY=-14 EndZ=0
    g13: LineSegment StartX=-12.8401 StartY=-16 StartZ=0 EndX=-12.8401 EndY=-17.6958 EndZ=0
    g14: LineSegment StartX=-10.15 StartY=-12 StartZ=0 EndX=-7.79258 EndY=-12 EndZ=0
    g15: Circle CenterX=-6.2215 CenterY=-2 CenterZ=0 NormalX=0 NormalY=0 NormalZ=1 AngleXU=0 Radius=1
    g16: Circle CenterX=-6.22762 CenterY=-2.58724 CenterZ=0 NormalX=0 NormalY=0 NormalZ=1 AngleXU=0 Radius=1
    g17: Circle CenterX=-6.32538 CenterY=-4 CenterZ=0 NormalX=0 NormalY=0 NormalZ=1 AngleXU=0 Radius=1
    g18: BSplineCurve PolesCount=3 KnotsCount=2 Degree=2 IsPeriodic=0
    g19: GeomPoint X=-6.2215 Y=-2 Z=0
    g20: GeomPoint X=-6.32538 Y=-4 Z=0
    g21: Circle CenterX=-6.48644 CenterY=-5.99526 CenterZ=0 NormalX=0 NormalY=0 NormalZ=1 AngleXU=0 Radius=1
    g22: Circle CenterX=-6.58486 CenterY=-6.99526 CenterZ=0 NormalX=0 NormalY=0 NormalZ=1 AngleXU=0 Radius=1
    g23: Circle CenterX=-6.77343 CenterY=-8 CenterZ=0 NormalX=0 NormalY=0 NormalZ=1 AngleXU=0 Radius=1
    g24: BSplineCurve PolesCount=3 KnotsCount=2 Degree=2 IsPeriodic=0
    g25: GeomPoint X=-6.48644 Y=-5.99526 Z=0
    g26: GeomPoint X=-6.77343 Y=-8 Z=0
    g27: Circle CenterX=-7.19003 CenterY=-10 CenterZ=0 NormalX=0 NormalY=0 NormalZ=1 AngleXU=0 Radius=1
    g28: Circle CenterX=-7.44407 CenterY=-11.0915 CenterZ=0 NormalX=0 NormalY=0 NormalZ=1 AngleXU=0 Radius=1
    g29: Circle CenterX=-7.79258 CenterY=-12 CenterZ=0 NormalX=0 NormalY=0 NormalZ=1 AngleXU=0 Radius=1
    g30: BSplineCurve PolesCount=3 KnotsCount=2 Degree=2 IsPeriodic=0
    g31: GeomPoint X=-7.19003 Y=-10 Z=0
    g32: GeomPoint X=-7.79258 Y=-12 Z=0
    g33: Circle CenterX=-8.70761 CenterY=-14 CenterZ=0 NormalX=0 NormalY=0 NormalZ=1 AngleXU=0 Radius=1
    g34: Circle CenterX=-9.33087 CenterY=-15.1837 CenterZ=0 NormalX=0 NormalY=0 NormalZ=1 AngleXU=0 Radius=1
    g35: Circle CenterX=-10.1571 CenterY=-16 CenterZ=0 NormalX=0 NormalY=0 NormalZ=1 AngleXU=0 Radius=1
    g36: BSplineCurve PolesCount=3 KnotsCount=2 Degree=2 IsPeriodic=0
    g37: GeomPoint X=-8.70761 Y=-14 Z=0
    g38: GeomPoint X=-10.1571 Y=-16 Z=0
    g39: Circle CenterX=-12.8401 CenterY=-17.6958 CenterZ=0 NormalX=0 NormalY=0 NormalZ=1 AngleXU=0 Radius=1
    g40: Circle CenterX=-13.3521 CenterY=-17.9027 CenterZ=0 NormalX=0 NormalY=0 NormalZ=1 AngleXU=0 Radius=1
    g41: Circle CenterX=-14 CenterY=-18 CenterZ=0 NormalX=0 NormalY=0 NormalZ=1 AngleXU=0 Radius=1
    g42: BSplineCurve PolesCount=3 KnotsCount=2 Degree=2 IsPeriodic=0
    g43: GeomPoint X=-12.8401 Y=-17.6958 Z=0
    g44: GeomPoint X=-14 Y=-18 Z=0
    g45: LineSegment StartX=-6.2 StartY=0 StartZ=0 EndX=-7.2 EndY=0 EndZ=0
    g46: LineSegment StartX=-7.2 StartY=0 StartZ=0 EndX=-7.2 EndY=-2 EndZ=0
    g47: LineSegment StartX=-7.2 StartY=-2 StartZ=0 EndX=-6.2215 EndY=-2 EndZ=0
    g48: LineSegment StartX=-6.32538 StartY=-4 StartZ=0 EndX=-7.65538 EndY=-4 EndZ=0
    g49: LineSegment StartX=-7.65538 StartY=-4 StartZ=0 EndX=-7.65538 EndY=-5.99526 EndZ=0
    g50: LineSegment StartX=-7.65538 StartY=-5.99526 StartZ=0 EndX=-6.48644 EndY=-5.99526 EndZ=0
    g51: LineSegment StartX=-6.77343 StartY=-8 StartZ=0 EndX=-8.43343 EndY=-8 EndZ=0
    g52: LineSegment StartX=-8.43343 StartY=-8 StartZ=0 EndX=-8.43343 EndY=-10 EndZ=0
    g53: LineSegment StartX=-8.43343 StartY=-10 StartZ=0 EndX=-7.19003 EndY=-10 EndZ=0
  constraints (112):
    c: Horizontal(g0)
    c: Distance(g0) = 2
    c: Block(g0)
    c: Vertical(g1)
    c: Coincident(g2,g0)
    c: Vertical(g2)
    c: Block(g2)
    c: Coincident(g6,g2)
    c: Weight(g3) = 1
    c: Equal(g3,g4)
    c: Equal(g3,g5)
    c: InternalAlignment(g3,g6)
    c: InternalAlignment(g4,g6)
    c: InternalAlignment(g5,g6)
    c: InternalAlignment(g7,g6)
    c: InternalAlignment(g8,g6)
    c: Block(g6)
    c: Coincident(g9,g1)
    c: Coincident(g9,g6)
    c: Horizontal(g9)
    c: Vertical(g10)
    c: Block(g10)
    c: Horizontal(g11)
    c: Block(g11)
    c: Coincident(g12,g10)
    c: Horizontal(g12)
    c: Block(g12)
    c: Coincident(g13,g11)
    c: Vertical(g13)
    c: Block(g13)
    c: Coincident(g14,g10)
    c: Horizontal(g14)
    c: Block(g14)
    c: Block(g9)
    c: Block(g1)
    c: Weight(g15) = 1
    c: Equal(g15,g16)
    c: Equal(g15,g17)
    c: InternalAlignment(g15,g18)
    c: InternalAlignment(g16,g18)
    c: InternalAlignment(g17,g18)
    c: InternalAlignment(g19,g18)
    c: InternalAlignment(g20,g18)
    c: Weight(g21) = 1
    c: Equal(g21,g22)
    c: Equal(g21,g23)
    c: InternalAlignment(g21,g24)
    c: InternalAlignment(g22,g24)
    c: InternalAlignment(g23,g24)
    c: InternalAlignment(g25,g24)
    c: InternalAlignment(g26,g24)
    c: Weight(g27) = 1
    c: Equal(g27,g28)
    c: Equal(g27,g29)
    c: Coincident(g30,g14)
    c: InternalAlignment(g27,g30)
    c: InternalAlignment(g28,g30)
    c: InternalAlignment(g29,g30)
    c: InternalAlignment(g31,g30)
    c: InternalAlignment(g32,g30)
    c: Coincident(g36,g12)
    c: Weight(g33) = 1
    c: Equal(g33,g34)
    c: Equal(g33,g35)
    c: Coincident(g36,g11)
    c: InternalAlignment(g33,g36)
    c: InternalAlignment(g34,g36)
    c: InternalAlignment(g35,g36)
    c: InternalAlignment(g37,g36)
    c: InternalAlignment(g38,g36)
    c: Coincident(g42,g13)
    c: Weight(g39) = 1
    c: Equal(g39,g40)
    c: Equal(g39,g41)
    c: Coincident(g42,g1)
    c: InternalAlignment(g39,g42)
    c: InternalAlignment(g40,g42)
    c: InternalAlignment(g41,g42)
    c: InternalAlignment(g43,g42)
    c: InternalAlignment(g44,g42)
    c: Block(g18)
    c: Block(g24)
    c: Block(g30)
    c: Block(g36)
    c: Block(g42)
    c: Horizontal(g45)
    c: Coincident(g45,g0)
    c: Vertical(g46)
    c: Coincident(g46,g45)
    c: Coincident(g47,g46)
    c: Coincident(g47,g18)
    c: Horizontal(g47)
    c: Block(g46)
    c: Coincident(g48,g18)
    c: Horizontal(g48)
    c: Distance(g48) = 1.33
    c: Vertical(g49)
    c: Coincident(g49,g48)
    c: Coincident(g50,g49)
    c: Coincident(g50,g24)
    c: Horizontal(g50)
    c: Tangent(g50,g22)
    c: Horizontal(g51)
    c: Coincident(g51,g24)
    c: Block(g51)
    c: Vertical(g52)
    c: Block(g52)
    c: Coincident(g52,g51)
    c: Coincident(g53,g52)
    c: Coincident(g53,g30)
    c: Horizontal(g53)
    c: Distance(g1) = 8.5
FEATURE [Part::Feature] Face024
  shape: bbox 9.8 x 26.5 x 2e-07 mm, 1 faces, 0 solids (baked)
FEATURE [Part::Revolution] Revolve024
  Angle = 360
  Axis = (0,1,0)
  Base = (0,0,0)
  FaceMakerClass = Part::FaceMakerBullseye
  Placement = pos=(0,0,0) rot=(0,0,1;1.5708rad)
  Solid = false
  Source = -> Face024
  Symmetric = false
FEATURE [Part::Feature] Face025
  shape: bbox 9.8 x 26.5 x 2e-07 mm, 1 faces, 0 solids (baked)
FEATURE [Part::Revolution] Revolve025
  Angle = 360
  Axis = (0,1,0)
  Base = (0,0,0)
  FaceMakerClass = Part::FaceMakerBullseye
  Placement = pos=(0,0,0) rot=(0,0,1;1.5708rad)
  Solid = false
  Source = -> Face025
  Symmetric = false
FEATURE [Part::MultiFuse] Fusion033
  Placement = pos=(-18,19,36) rot=(0,0,1;0rad)
  Shapes = -> [Revolve025,Revolve024]
FEATURE [Part::Cylinder] Cylinder014
  Angle = 360
  AttacherType = Attacher::AttachEngine3D
  Height = 20
  Placement = pos=(0,0,36.15) rot=(0,0,1;0rad)
  Radius = 14.3
FEATURE [Part::Cylinder] Cylinder015
  Angle = 360
  AttacherType = Attacher::AttachEngine3D
  Height = 10
  Placement = pos=(0,0,36.15) rot=(0,0,1;0rad)
  Radius = 4
FEATURE [Part::MultiFuse] Fusion034  label="removeToCreteHoleForPlugHousing004"
  Placement = pos=(-42,19,36) rot=(0,1,0;1.5708rad)
  Shapes = -> [Cylinder014,Cylinder015]
FEATURE [Part::Cut] Cut008  label="top004"
  Base = -> Cut004
  Placement = pos=(-1,0,0) rot=(0,0,1;0rad)
  Tool = -> Fusion034
FEATURE [Part::Box] Box005  label="Cube005"
  AttacherType = Attacher::AttachEngine3D
  Height = 28
  Length = 3
  Placement = pos=(110.7,19,22) rot=(0,0,1;0rad)
  Width = 15.7
FEATURE [Part::Cylinder] Cylinder016
  Angle = 360
  AttacherType = Attacher::AttachEngine3D
  Height = 10
  Placement = pos=(0,0,36.15) rot=(0,0,1;0rad)
  Radius = 4
FEATURE [Part::Cylinder] Cylinder017
  Angle = 360
  AttacherType = Attacher::AttachEngine3D
  Height = 20
  Placement = pos=(0,0,36.15) rot=(0,0,1;0rad)
  Radius = 10.3
FEATURE [Part::MultiFuse] Fusion035  label="removeToCreteHoleForPlugHousing005"
  Placement = pos=(70,19,36) rot=(0,1,0;1.5708rad)
  Shapes = -> [Cylinder017,Cylinder016]
FEATURE [Part::Cut] Cut009  label="plugHousingTab001"
  Base = -> Box005
  Placement = pos=(-107.4,-14,0) rot=(0,0,1;0rad)
  Tool = -> Fusion035
FEATURE [Part::Box] Box006  label="Cube006"
  AttacherType = Attacher::AttachEngine3D
  Height = 28
  Length = 3
  Placement = pos=(110.7,19,22) rot=(0,0,1;0rad)
  Width = 15.7
FEATURE [Part::Cylinder] Cylinder018
  Angle = 360
  AttacherType = Attacher::AttachEngine3D
  Height = 10
  Placement = pos=(0,0,36.15) rot=(0,0,1;0rad)
  Radius = 4
FEATURE [Part::Cylinder] Cylinder019
  Angle = 360
  AttacherType = Attacher::AttachEngine3D
  Height = 20
  Placement = pos=(0,0,36.15) rot=(0,0,1;0rad)
  Radius = 10.3
FEATURE [Part::MultiFuse] Fusion036  label="removeToCreteHoleForPlugHousing006"
  Placement = pos=(70,19,36) rot=(0,1,0;1.5708rad)
  Shapes = -> [Cylinder019,Cylinder018]
FEATURE [Part::Cut] Cut010  label="plugHousingTab002"
  Base = -> Box006
  Placement = pos=(-107.4,-14,0) rot=(0,0,1;0rad)
  Tool = -> Fusion036
FEATURE [Part::MultiFuse] Fusion037
  Placement = pos=(9.6,23,0) rot=(0,0,1;3.14159rad)
  Shapes = -> [Cut009,Cut010]
FEATURE [Part::Box] Box  label="Cube"
  AttacherType = Attacher::AttachEngine3D
  Height = 10
  Length = 3
  Placement = pos=(3.3,4,12) rot=(0,0,1;0rad)
  Width = 10
FEATURE [Part::Fillet] Fillet004
  Base = -> Fusion028
  Edges = 1 edges r=2: [Edge25]
FEATURE [Part::Fillet] Fillet005  label="plugHousing046"
  Base = -> Fillet004
  Edges = 1 edges r=2: [Edge8]
FEATURE [Part::Fillet] Fillet006
  Base = -> Box
  Edges = 1 edges r=2: [Edge11]
FEATURE [Part::Box] Box007  label="Cube007"
  AttacherType = Attacher::AttachEngine3D
  Height = 10
  Length = 3
  Placement = pos=(3.3,4,50) rot=(0,0,1;0rad)
  Width = 10
FEATURE [Part::Fillet] Fillet007
  Base = -> Box007
  Edges = 1 edges r=2: [Edge12]
FEATURE [Part::Box] Box008  label="Cube008"
  AttacherType = Attacher::AttachEngine3D
  Height = 28
  Length = 4
  Placement = pos=(5,0,22) rot=(0,0,1;0rad)
  Width = 10
FEATURE [Part::Fillet] Fillet008
  Base = -> Box008
  Edges = 1 edges r=1: [Edge7]
FEATURE [Part::Fillet] Fillet009
  Base = -> Fillet008
  Edges = 1 edges r=2: [Edge5]
FEATURE [Part::Fillet] Fillet010
  Base = -> Fillet009
  Edges = 1 edges r=2: [Edge2]
FEATURE [Sketcher::SketchObject] Sketch009  label="topSketch003"
  FullyConstrained = true
  sketch-geometry (4):
    g0: LineSegment StartX=16.8446 StartY=31.512 StartZ=0 EndX=16.3251 EndY=34.4666 EndZ=0
    g1: ArcOfCircle CenterX=19 CenterY=19.2524 CenterZ=0 NormalX=0 NormalY=0 NormalZ=1 AngleXU=0 Radius=15.4476 StartAngle=1.74483 EndAngle=2.72717
    g2: ArcOfCircle CenterX=19 CenterY=19.2524 CenterZ=0 NormalX=0 NormalY=0 NormalZ=1 AngleXU=0 Radius=12.4476 StartAngle=1.74483 EndAngle=2.73189
    g3: LineSegment StartX=4.86004 StartY=25.4725 StartZ=0 EndX=7.58253 EndY=24.2107 EndZ=0
  constraints (7):
    c: Block(g0)
    c: Coincident(g1,g0)
    c: Coincident(g2,g0)
    c: Coincident(g3,g1)
    c: Coincident(g3,g2)
    c: Block(g1)
    c: Block(g2)
FEATURE [Part::Extrusion] Extrude008
  Base = -> Sketch009
  Dir = (0,0,1)
  DirMode = 2
  FaceMakerClass = Part::FaceMakerBullseye
  LengthFwd = 10
  LengthRev = 0
  Placement = pos=(0,0,31) rot=(0,0,1;0rad)
  Solid = true
  Symmetric = false
FEATURE [Part::Cylinder] Cylinder020
  Angle = 360
  AttacherType = Attacher::AttachEngine3D
  Height = 20
  Placement = pos=(0,0,36.15) rot=(0,0,1;0rad)
  Radius = 8.2
FEATURE [Part::Cylinder] Cylinder021
  Angle = 360
  AttacherType = Attacher::AttachEngine3D
  Height = 10
  Placement = pos=(0,0,36.15) rot=(0,0,1;0rad)
  Radius = 4
FEATURE [Part::MultiFuse] Fusion038  label="removeToCreteHoleForPlugHousing007"
  Placement = pos=(-42,19,36) rot=(0,1,0;1.5708rad)
  Shapes = -> [Cylinder020,Cylinder021]
FEATURE [Part::Cut] Cut011
  Base = -> Extrude008
  Tool = -> Fusion038
FEATURE [Part::Fillet] Fillet011
  Base = -> Cut011
  Edges = 1 edges r=2: [Edge1]
FEATURE [Part::Fillet] Fillet012
  Base = -> Fillet011
  Edges = 1 edges r=2.5: [Edge1]
FEATURE [Part::Fillet] Fillet013
  Base = -> Fillet012
  Edges = 1 edges r=2.5: [Edge2]
FEATURE [Part::Box] Box010  label="Cube010"
  AttacherType = Attacher::AttachEngine3D
  Height = 16
  Length = 8
  Placement = pos=(12.7,31.52,28) rot=(0,0,1;0rad)
  Width = 4
FEATURE [Sketcher::SketchObject] Sketch010  label="topSketch004"
  FullyConstrained = true
  sketch-geometry (4):
    g0: LineSegment StartX=16.8446 StartY=31.512 StartZ=0 EndX=16.3251 EndY=34.4666 EndZ=0
    g1: ArcOfCircle CenterX=19 CenterY=19.2524 CenterZ=0 NormalX=0 NormalY=0 NormalZ=1 AngleXU=0 Radius=15.4476 StartAngle=1.74483 EndAngle=2.72717
    g2: ArcOfCircle CenterX=19 CenterY=19.2524 CenterZ=0 NormalX=0 NormalY=0 NormalZ=1 AngleXU=0 Radius=12.4476 StartAngle=1.74483 EndAngle=2.73189
    g3: LineSegment StartX=4.86004 StartY=25.4725 StartZ=0 EndX=7.58253 EndY=24.2107 EndZ=0
  constraints (7):
    c: Block(g0)
    c: Coincident(g1,g0)
    c: Coincident(g2,g0)
    c: Coincident(g3,g1)
    c: Coincident(g3,g2)
    c: Block(g1)
    c: Block(g2)
FEATURE [Part::Cylinder] Cylinder022
  Angle = 360
  AttacherType = Attacher::AttachEngine3D
  Height = 10
  Placement = pos=(0,0,36.15) rot=(0,0,1;0rad)
  Radius = 4
FEATURE [Sketcher::SketchObject] Sketch011  label="topSketch005"
  FullyConstrained = true
  sketch-geometry (4):
    g0: LineSegment StartX=16.8446 StartY=31.512 StartZ=0 EndX=16.3251 EndY=34.4666 EndZ=0
    g1: ArcOfCircle CenterX=19 CenterY=19.2524 CenterZ=0 NormalX=0 NormalY=0 NormalZ=1 AngleXU=0 Radius=15.4476 StartAngle=1.74483 EndAngle=2.72717
    g2: ArcOfCircle CenterX=19 CenterY=19.2524 CenterZ=0 NormalX=0 NormalY=0 NormalZ=1 AngleXU=0 Radius=12.4476 StartAngle=1.74483 EndAngle=2.73189
    g3: LineSegment StartX=4.86004 StartY=25.4725 StartZ=0 EndX=7.58253 EndY=24.2107 EndZ=0
  constraints (7):
    c: Block(g0)
    c: Coincident(g1,g0)
    c: Coincident(g2,g0)
    c: Coincident(g3,g1)
    c: Coincident(g3,g2)
    c: Block(g1)
    c: Block(g2)
FEATURE [Part::Extrusion] Extrude010
  Base = -> Sketch011
  Dir = (0,0,1)
  DirMode = 2
  FaceMakerClass = Part::FaceMakerBullseye
  LengthFwd = 10.6
  LengthRev = 0
  Placement = pos=(0,0,31) rot=(0,0,1;0rad)
  Solid = true
  Symmetric = false
FEATURE [Part::Cylinder] Cylinder023
  Angle = 360
  AttacherType = Attacher::AttachEngine3D
  Height = 20
  Placement = pos=(0,0,36.15) rot=(0,0,1;0rad)
  Radius = 8.2
FEATURE [Part::MultiFuse] Fusion039  label="removeToCreteHoleForPlugHousing008"
  Placement = pos=(-42,19,36) rot=(0,1,0;1.5708rad)
  Shapes = -> [Cylinder023,Cylinder022]
FEATURE [Part::Cut] Cut012
  Base = -> Extrude010
  Placement = pos=(0,0,-0.3) rot=(0,0,1;0rad)
  Tool = -> Fusion039
FEATURE [Part::Cut] Cut013
  Base = -> Box010
  Tool = -> Cut012
FEATURE [Part::Fillet] Fillet014
  Base = -> Cut013
  Edges = 1 edges r=0.7: [Edge13]
FEATURE [Part::Fillet] Fillet015
  Base = -> Fillet014
  Edges = 1 edges r=0.7: [Edge13]
FEATURE [Part::Fillet] Fillet016
  Base = -> Fillet015
  Edges = 1 edges r=0.7: [Edge16]
FEATURE [Part::Fillet] Fillet017
  Base = -> Fillet016
  Edges = 1 edges r=0.7: [Edge11]
FEATURE [Part::Fillet] Fillet018
  Base = -> Fillet017
  Edges = 1 edges r=0.7: [Edge10]
FEATURE [Part::Fillet] Fillet019
  Base = -> Fillet018
  Edges = 1 edges r=1.2: [Edge5]
FEATURE [Part::Fillet] Fillet020
  Base = -> Fillet019
  Edges = 1 edges r=1.2: [Edge12]
FEATURE [Part::Fillet] Fillet021
  Base = -> Fillet020
  Edges = 1 edges r=2: [Edge1]
  Placement = pos=(0.3,0,0) rot=(0,0,1;0rad)
FEATURE [Part::MultiFuse] Fusion040  label="top005"
  Shapes = -> [Cut008,Fillet021]
FEATURE [Part::MultiFuse] Fusion041  label="wireHolder"
  Shapes = -> [Fusion033,Fillet013]
FEATURE [Part::MultiFuse] Fusion042
  Shapes = -> [Fillet007,Fusion041]
FEATURE [Part::MultiFuse] Fusion043  label="wireHolder001"
  Shapes = -> [Fusion042,Fillet010]
FEATURE [Part::MultiFuse] Fusion044  label="wireHolder002"
  Shapes = -> [Fillet006,Fusion037,Fusion043]
FEATURE [Part::Feature] Face026
  shape: bbox 11 x 6 x 2e-07 mm, 1 faces, 0 solids (baked)
FEATURE [Part::Revolution] Revolve026
  Angle = 360
  Axis = (0,1,0)
  Base = (0,0,0)
  FaceMakerClass = Part::FaceMakerBullseye
  Placement = pos=(30.3,-1,19.7) rot=(0,0,1;0rad)
  Solid = false
  Source = -> Face026
  Symmetric = false
FEATURE [Sketcher::SketchObject] Sketch013  label="topSketch006"
  FullyConstrained = true
  sketch-geometry (13):
    g0: LineSegment StartX=117 StartY=19 StartZ=0 EndX=117 EndY=38 EndZ=0
    g1: ArcOfCircle CenterX=98 CenterY=19 CenterZ=0 NormalX=0 NormalY=0 NormalZ=1 AngleXU=0 Radius=19 StartAngle=5.7297 EndAngle=6.28319
    g2: LineSegment StartX=0 StartY=3 StartZ=0 EndX=0 EndY=19 EndZ=0
    g3: LineSegment StartX=19 StartY=38 StartZ=0 EndX=117 EndY=38 EndZ=0
    g4: ArcOfCircle CenterX=19 CenterY=19 CenterZ=0 NormalX=0 NormalY=0 NormalZ=1 AngleXU=0 Radius=19 StartAngle=1.5708 EndAngle=3.14159
    g5: ArcOfCircle CenterX=19 CenterY=19 CenterZ=0 NormalX=0 NormalY=0 NormalZ=1 AngleXU=0 Radius=16 StartAngle=1.5708 EndAngle=3.14159
    g6: ArcOfCircle CenterX=98 CenterY=19 CenterZ=0 NormalX=0 NormalY=0 NormalZ=1 AngleXU=0 Radius=16 StartAngle=5.60905 EndAngle=6.28319
    g7: LineSegment StartX=114 StartY=19 StartZ=0 EndX=114 EndY=35 EndZ=0
    g8: LineSegment StartX=110.5 StartY=9.01251 StartZ=0 EndX=114.163 EndY=9.01251 EndZ=0
    g9: LineSegment StartX=114 StartY=35 StartZ=0 EndX=19 EndY=35 EndZ=0
    g10: LineSegment StartX=0 StartY=3 StartZ=0 EndX=0 EndY=0 EndZ=0
    g11: LineSegment StartX=3 StartY=0 StartZ=0 EndX=0 EndY=0 EndZ=0
    g12: LineSegment StartX=3 StartY=19 StartZ=0 EndX=3 EndY=0 EndZ=0
  constraints (33):
    c: Vertical(g0)
    c: Distance(g0) = 19
    c: Block(g0)
    c: Coincident(g1,g0)
    c: Block(g1)
    c: Vertical(g2)
    c: Block(g2)
    c: Coincident(g3,g0)
    c: Horizontal(g3)
    c: Distance(g3) = 98
    c: Coincident(g4,g3)
    c: Coincident(g4,g2)
    c: Block(g4)
    c: Coincident(g5,g4)
    c: Coincident(g6,g1)
    c: Block(g6)
    c: Block(g5)
    c: Coincident(g7,g6)
    c: Vertical(g7)
    c: Coincident(g8,g6)
    c: Coincident(g8,g1)
    c: Coincident(g9,g7)
    c: Coincident(g9,g5)
    c: Horizontal(g9)
    c: Tangent(g9,g5)
    c: Coincident(g10,g2)
    c: Distance(g10) = 3
    c: Vertical(g10)
    c: Coincident(g11,g10)
    c: Horizontal(g11)
    c: Coincident(g12,g5)
    c: Coincident(g12,g11)
    c: Vertical(g12)
FEATURE [Part::Extrusion] Extrude011  label="top006"
  Base = -> Sketch013
  Dir = (0,0,1)
  DirMode = 2
  FaceMakerClass = Part::FaceMakerBullseye
  LengthFwd = 72
  LengthRev = 0
  Solid = true
  Symmetric = false
FEATURE [Sketcher::SketchObject] Sketch014
  FullyConstrained = true
  MapMode = 3
  Placement = pos=(0,0,0) rot=(1,0,0;1.5708rad)
  Support = -> [Extrude011]
  sketch-geometry (8):
    g0: Circle CenterX=80.351 CenterY=-67.6202 CenterZ=0 NormalX=0 NormalY=0 NormalZ=1 AngleXU=0 Radius=2
    g1: Circle CenterX=80.351 CenterY=-67.6202 CenterZ=0 NormalX=0 NormalY=0 NormalZ=1 AngleXU=0 Radius=3
    g2: Circle CenterX=80.351 CenterY=-4.92017 CenterZ=0 NormalX=0 NormalY=0 NormalZ=1 AngleXU=0 Radius=2
    g3: Circle CenterX=80.351 CenterY=-4.92017 CenterZ=0 NormalX=0 NormalY=0 NormalZ=1 AngleXU=0 Radius=3
    g4: Circle CenterX=23.851 CenterY=-4.92017 CenterZ=0 NormalX=0 NormalY=0 NormalZ=1 AngleXU=0 Radius=2
    g5: Circle CenterX=23.851 CenterY=-4.92017 CenterZ=0 NormalX=0 NormalY=0 NormalZ=1 AngleXU=0 Radius=3
    g6: Circle CenterX=23.851 CenterY=-67.6202 CenterZ=0 NormalX=0 NormalY=0 NormalZ=1 AngleXU=0 Radius=2
    g7: Circle CenterX=23.851 CenterY=-67.6202 CenterZ=0 NormalX=0 NormalY=0 NormalZ=1 AngleXU=0 Radius=3
  constraints (8):
    c: Block(g3)
    c: Block(g2)
    c: Block(g1)
    c: Block(g0)
    c: Block(g6)
    c: Block(g7)
    c: Block(g4)
    c: Block(g5)
FEATURE [Part::Feature] Face027
  shape: bbox 11 x 6 x 2e-07 mm, 1 faces, 0 solids (baked)
FEATURE [Part::Revolution] Revolve027
  Angle = 360
  Axis = (0,1,0)
  Base = (0,0,0)
  FaceMakerClass = Part::FaceMakerBullseye
  Placement = pos=(30.3,-1,51.7) rot=(0,0,1;0rad)
  Solid = false
  Source = -> Face027
  Symmetric = false
FEATURE [Part::Feature] Face028
  shape: bbox 11 x 6 x 2e-07 mm, 1 faces, 0 solids (baked)
FEATURE [Part::Revolution] Revolve028
  Angle = 360
  Axis = (0,1,0)
  Base = (0,0,0)
  FaceMakerClass = Part::FaceMakerBullseye
  Placement = pos=(62.3,-1,19.7) rot=(0,0,1;0rad)
  Solid = false
  Source = -> Face028
  Symmetric = false
FEATURE [Part::Feature] Face029
  shape: bbox 11 x 6 x 2e-07 mm, 1 faces, 0 solids (baked)
FEATURE [Part::Revolution] Revolve029
  Angle = 360
  Axis = (0,1,0)
  Base = (0,0,0)
  FaceMakerClass = Part::FaceMakerBullseye
  Placement = pos=(62.3,-1,51.7) rot=(0,0,1;0rad)
  Solid = false
  Source = -> Face029
  Symmetric = false
FEATURE [Part::Feature] Wire
  shape: bbox 11 x 5.2 x 2e-07 mm, 0 faces, 0 solids (baked)
FEATURE [Part::Revolution] Revolve030
  Angle = 360
  Axis = (0,1,0)
  Base = (0,0,0)
  FaceMakerClass = Part::FaceMakerBullseye
  Placement = pos=(30.3,38,19.7) rot=(0,0,1;0rad)
  Solid = true
  Source = -> Wire
  Symmetric = false
FEATURE [Part::Feature] Wire001
  shape: bbox 11 x 5.2 x 2e-07 mm, 0 faces, 0 solids (baked)
FEATURE [Part::Revolution] Revolve031
  Angle = 360
  Axis = (0,1,0)
  Base = (0,0,0)
  FaceMakerClass = Part::FaceMakerBullseye
  Placement = pos=(30.3,38,51.7) rot=(0,0,1;0rad)
  Solid = true
  Source = -> Wire001
  Symmetric = false
FEATURE [Part::Feature] Wire002
  shape: bbox 11 x 5.2 x 2e-07 mm, 0 faces, 0 solids (baked)
FEATURE [Part::Revolution] Revolve032
  Angle = 360
  Axis = (0,1,0)
  Base = (0,0,0)
  FaceMakerClass = Part::FaceMakerBullseye
  Placement = pos=(62.3,38,51.7) rot=(0,0,1;0rad)
  Solid = true
  Source = -> Wire002
  Symmetric = false
FEATURE [Part::Feature] Wire003
  shape: bbox 11 x 5.2 x 2e-07 mm, 0 faces, 0 solids (baked)
FEATURE [Part::Revolution] Revolve033
  Angle = 360
  Axis = (0,1,0)
  Base = (0,0,0)
  FaceMakerClass = Part::FaceMakerBullseye
  Placement = pos=(62.3,38,19.7) rot=(0,0,1;0rad)
  Solid = true
  Source = -> Wire003
  Symmetric = false
FEATURE [Part::MultiFuse] Fusion045  label="altRandScrewHousing"
  Shapes = -> [Revolve029,Revolve027,Revolve028,Revolve026]
FEATURE [Part::MultiFuse] Fusion046  label="fanScrewHousing"
  Shapes = -> [Revolve033,Revolve032,Revolve031,Revolve030]
FEATURE [Sketcher::SketchObject] Sketch015
  FullyConstrained = true
  sketch-geometry (17):
    g0: Circle CenterX=-3.5 CenterY=23.5 CenterZ=0 NormalX=0 NormalY=0 NormalZ=1 AngleXU=0 Radius=1
    g1: Circle CenterX=-1 CenterY=15.25 CenterZ=0 NormalX=0 NormalY=0 NormalZ=1 AngleXU=0 Radius=1
    g2: Circle CenterX=-3.5 CenterY=7 CenterZ=0 NormalX=0 NormalY=0 NormalZ=1 AngleXU=0 Radius=1
    g3: BSplineCurve PolesCount=3 KnotsCount=2 Degree=2 IsPeriodic=0
    g4: GeomPoint X=-3.5 Y=23.5 Z=0
    g5: GeomPoint X=-3.5 Y=7 Z=0
    g6: Circle CenterX=-4.8 CenterY=30.5 CenterZ=0 NormalX=0 NormalY=0 NormalZ=1 AngleXU=0 Radius=1
    g7: Circle CenterX=-3.5 CenterY=30.5 CenterZ=0 NormalX=0 NormalY=0 NormalZ=1 AngleXU=0 Radius=1
    g8: Circle CenterX=-3.5 CenterY=29.2 CenterZ=0 NormalX=0 NormalY=0 NormalZ=1 AngleXU=0 Radius=1
    g9: BSplineCurve PolesCount=3 KnotsCount=2 Degree=2 IsPeriodic=0
    g10: GeomPoint X=-4.8 Y=30.5 Z=0
    g11: GeomPoint X=-3.5 Y=29.2 Z=0
    g12: LineSegment StartX=-3.5 StartY=29.2 StartZ=0 EndX=-3.5 EndY=23.5 EndZ=0
    g13: LineSegment StartX=-4.8 StartY=30.5 StartZ=0 EndX=0 EndY=30.5 EndZ=0
    g14: LineSegment StartX=-3.5 StartY=0.3 StartZ=0 EndX=0 EndY=0.3 EndZ=0
    g15: LineSegment StartX=-3.5 StartY=0.3 StartZ=0 EndX=-3.5 EndY=7 EndZ=0
    g16: LineSegment StartX=0 StartY=0.3 StartZ=0 EndX=0 EndY=30.5 EndZ=0
  constraints (33):
    c: Weight(g0) = 1
    c: Equal(g0,g1)
    c: Equal(g0,g2)
    c: InternalAlignment(g0,g3)
    c: InternalAlignment(g1,g3)
    c: InternalAlignment(g2,g3)
    c: InternalAlignment(g4,g3)
    c: InternalAlignment(g5,g3)
    c: Block(g3)
    c: Weight(g6) = 1
    c: Equal(g6,g7)
    c: Equal(g6,g8)
    c: InternalAlignment(g6,g9)
    c: InternalAlignment(g7,g9)
    c: InternalAlignment(g8,g9)
    c: InternalAlignment(g10,g9)
    c: InternalAlignment(g11,g9)
    c: Block(g9)
    c: Coincident(g12,g9)
    c: Coincident(g12,g3)
    c: Vertical(g12)
    c: Coincident(g13,g9)
    c: Horizontal(g13)
    c: Distance(g13) = 4.8
    c: Horizontal(g14)
    c: Block(g14)
    c: Coincident(g15,g14)
    c: Coincident(g15,g3)
    c: Vertical(g15)
    c: Coincident(g16,g14)
    c: Coincident(g16,g13)
    c: Vertical(g16)
    c: Tangent(g16,g1)
FEATURE [Sketcher::SketchObject] Sketch016
  FullyConstrained = true
  sketch-geometry (16):
    g0: Circle CenterX=-3.5 CenterY=23.5 CenterZ=0 NormalX=0 NormalY=0 NormalZ=1 AngleXU=0 Radius=1
    g1: Circle CenterX=-1 CenterY=15.25 CenterZ=0 NormalX=0 NormalY=0 NormalZ=1 AngleXU=0 Radius=1
    g2: Circle CenterX=-3.5 CenterY=7 CenterZ=0 NormalX=0 NormalY=0 NormalZ=1 AngleXU=0 Radius=1
    g3: BSplineCurve PolesCount=3 KnotsCount=2 Degree=2 IsPeriodic=0
    g4: GeomPoint X=-3.5 Y=23.5 Z=0
    g5: GeomPoint X=-3.5 Y=7 Z=0
    g6: LineSegment StartX=-3.5 StartY=28.2 StartZ=0 EndX=-3.5 EndY=23.5 EndZ=0
    g7: LineSegment StartX=0 StartY=29.5 StartZ=0 EndX=0 EndY=30 EndZ=0
    g8: LineSegment StartX=-3.5 StartY=28.2 StartZ=0 EndX=-3.5 EndY=30 EndZ=0
    g9: LineSegment StartX=0 StartY=30 StartZ=0 EndX=0 EndY=30.5 EndZ=0
    g10: LineSegment StartX=0 StartY=30.5 StartZ=0 EndX=-3.5 EndY=30.5 EndZ=0
    g11: LineSegment StartX=-3.5 StartY=30.5 StartZ=0 EndX=-3.5 EndY=30 EndZ=0
    g12: LineSegment StartX=0 StartY=29.5 StartZ=0 EndX=0 EndY=5 EndZ=0
    g13: LineSegment StartX=-3.5 StartY=0.3 StartZ=0 EndX=-3.5 EndY=7 EndZ=0
    g14: LineSegment StartX=-3.5 StartY=0.3 StartZ=0 EndX=0 EndY=0.3 EndZ=0
    g15: LineSegment StartX=0 StartY=5 StartZ=0 EndX=0 EndY=0.3 EndZ=0
  constraints (39):
    c: Weight(g0) = 1
    c: Equal(g0,g1)
    c: Equal(g0,g2)
    c: InternalAlignment(g0,g3)
    c: InternalAlignment(g1,g3)
    c: InternalAlignment(g2,g3)
    c: InternalAlignment(g4,g3)
    c: InternalAlignment(g5,g3)
    c: Block(g3)
    c: Coincident(g6,g3)
    c: Vertical(g6)
    c: Vertical(g7)
    c: Distance(g7) = 0.5
    c: Coincident(g8,g6)
    c: Vertical(g8)
    c: Block(g6)
    c: Block(g7)
    c: Vertical(g9)
    c: Equal(g7,g9) = 0.5
    c: Block(g9)
    c: Coincident(g9,g7)
    c: Horizontal(g10)
    c: Coincident(g10,g9)
    c: Coincident(g11,g10)
    c: Coincident(g11,g8)
    c: Vertical(g11)
    c: Block(g11)
    c: Coincident(g12,g7)
    c: Vertical(g12)
    c: Coincident(g13,g3)
    c: Vertical(g13)
    c: Distance(g13) = 6.7
    c: Coincident(g14,g13)
    c: Horizontal(g14)
    c: Block(g14)
    c: Coincident(g15,g12)
    c: Coincident(g15,g14)
    c: Vertical(g15)
    c: Block(g15)
FEATURE [Sketcher::SketchObject] Sketch017
  FullyConstrained = true
  sketch-geometry (11):
    g0: LineSegment StartX=-3.5 StartY=1e-16 StartZ=0 EndX=-1.6 EndY=1e-16 EndZ=0
    g1: LineSegment StartX=-1.6 StartY=1e-16 StartZ=0 EndX=-1.6 EndY=1.5 EndZ=0
    g2: LineSegment StartX=-3.5 StartY=1.5 StartZ=0 EndX=-1.6 EndY=1.5 EndZ=0
    g3: LineSegment StartX=-3.5 StartY=1e-16 StartZ=0 EndX=-4.8 EndY=1e-16 EndZ=0
    g4: Circle CenterX=-3.5 CenterY=1.3 CenterZ=0 NormalX=0 NormalY=0 NormalZ=1 AngleXU=0 Radius=1
    g5: Circle CenterX=-3.5 CenterY=1e-16 CenterZ=0 NormalX=0 NormalY=0 NormalZ=1 AngleXU=0 Radius=1
    g6: Circle CenterX=-4.8 CenterY=1e-16 CenterZ=0 NormalX=0 NormalY=0 NormalZ=1 AngleXU=0 Radius=1
    g7: BSplineCurve PolesCount=3 KnotsCount=2 Degree=2 IsPeriodic=0
    g8: GeomPoint X=-3.5 Y=1.3 Z=0
    g9: GeomPoint X=-4.8 Y=1e-16 Z=0
    g10: LineSegment StartX=-3.5 StartY=1.3 StartZ=0 EndX=-3.5 EndY=1.5 EndZ=0
  constraints (24):
    c: Horizontal(g0)
    c: Distance(g0) = 1.9
    c: Block(g0)
    c: Coincident(g1,g0)
    c: Vertical(g1)
    c: Coincident(g2,g1)
    c: Horizontal(g2)
    c: Coincident(g3,g0)
    c: Horizontal(g3)
    c: Distance(g3) = 1.3
    c: Weight(g4) = 1
    c: Equal(g4,g5)
    c: Coincident(g5,g0)
    c: Equal(g4,g6)
    c: Coincident(g7,g3)
    c: InternalAlignment(g4,g7)
    c: InternalAlignment(g5,g7)
    c: InternalAlignment(g6,g7)
    c: InternalAlignment(g8,g7)
    c: InternalAlignment(g9,g7)
    c: Coincident(g10,g7)
    c: Coincident(g10,g2)
    c: Vertical(g10)
    c: Block(g10)
FEATURE [Part::Feature] Face035
  shape: bbox 3.2 x 1.5 x 2e-07 mm, 1 faces, 0 solids (baked)
FEATURE [Part::Revolution] Revolve039  label="backCaseScrewRetainer"
  Angle = 360
  Axis = (0,1,0)
  Base = (0,0,0)
  FaceMakerClass = Part::FaceMakerBullseye
  Placement = pos=(12.5,3,62) rot=(0,0,1;0rad)
  Solid = false
  Source = -> Face035
  Symmetric = false
FEATURE [Part::Feature] Face036
  shape: bbox 3.2 x 1.5 x 2e-07 mm, 1 faces, 0 solids (baked)
FEATURE [Part::Feature] Face039
  shape: bbox 4.8 x 30.2 x 2e-07 mm, 1 faces, 0 solids (baked)
FEATURE [Part::Revolution] Revolve043  label="frontCaseScrewPost002"
  Angle = 360
  Axis = (0,1,0)
  Base = (0,0,0)
  FaceMakerClass = Part::FaceMakerBullseye
  Placement = pos=(89.5,4.5,3.5) rot=(0,0,1;0rad)
  Solid = false
  Source = -> Face039
  Symmetric = false
FEATURE [Part::Feature] Face042
  shape: bbox 4.8 x 30.2 x 2e-07 mm, 1 faces, 0 solids (baked)
FEATURE [Part::Revolution] Revolve046  label="frontCaseScrewPost003"
  Angle = 360
  Axis = (0,1,0)
  Base = (0,0,0)
  FaceMakerClass = Part::FaceMakerBullseye
  Placement = pos=(89.5,4.5,68.5) rot=(0,0,1;0rad)
  Solid = false
  Source = -> Face042
  Symmetric = false
FEATURE [Part::Feature] Face043
  shape: bbox 3.2 x 1.5 x 2e-07 mm, 1 faces, 0 solids (baked)
FEATURE [Part::Revolution] Revolve047  label="frontCaseScrewRetainer002"
  Angle = 360
  Axis = (0,1,0)
  Base = (0,0,0)
  FaceMakerClass = Part::FaceMakerBullseye
  Placement = pos=(89.5,3,68.5) rot=(0,0,1;0rad)
  Solid = false
  Source = -> Face043
  Symmetric = false
FEATURE [Part::Feature] Face044
  shape: bbox 3.2 x 1.5 x 2e-07 mm, 1 faces, 0 solids (baked)
FEATURE [Part::Revolution] Revolve048  label="frontCaseScrewRetainer003"
  Angle = 360
  Axis = (0,1,0)
  Base = (0,0,0)
  FaceMakerClass = Part::FaceMakerBullseye
  Placement = pos=(89.5,3,3.5) rot=(0,0,1;0rad)
  Solid = false
  Source = -> Face044
  Symmetric = false
FEATURE [App::MeasureDistance] Distance002  label="Distance: 1.67 mm"
  Distance = 1.66921
  P1 = (99.2361,4.7524,71.7)
  P2 = (99.2347,6.42161,71.7)
FEATURE [Sketcher::SketchObject] Sketch018
  FullyConstrained = true
  sketch-geometry (7):
    g0: LineSegment StartX=0 StartY=0 StartZ=0 EndX=0 EndY=6 EndZ=0
    g1: Circle CenterX=0 CenterY=0 CenterZ=0 NormalX=0 NormalY=0 NormalZ=1 AngleXU=0 Radius=1
    g2: Circle CenterX=8 CenterY=6 CenterZ=0 NormalX=0 NormalY=0 NormalZ=1 AngleXU=0 Radius=1
    g3: BSplineCurve PolesCount=3 KnotsCount=2 Degree=2 IsPeriodic=0
    g4: GeomPoint X=0 Y=0 Z=0
    g5: GeomPoint X=8 Y=6 Z=0
    g6: LineSegment StartX=0 StartY=6 StartZ=0 EndX=8 EndY=6 EndZ=0
  constraints (14):
    c: Coincident(g0,g-1)
    c: Distance(g0) = 6
    c: Vertical(g0)
    c: Coincident(g3,g0)
    c: Weight(g1) = 1
    c: Equal(g1,g2)
    c: InternalAlignment(g1,g3)
    c: InternalAlignment(g2,g3)
    c: InternalAlignment(g4,g3)
    c: InternalAlignment(g5,g3)
    c: Block(g3)
    c: Coincident(g6,g0)
    c: Coincident(g6,g3)
    c: Horizontal(g6)
FEATURE [Part::Extrusion] Extrude012  label="caseScrewPillarBracket"
  Base = -> Sketch018
  Dir = (0,0,1)
  DirMode = 2
  FaceMakerClass = Part::FaceMakerBullseye
  LengthFwd = 2.4
  LengthRev = 0
  Placement = pos=(15.76,29,8.8) rot=(0,1,0;0rad)
  Solid = true
  Symmetric = false
FEATURE [Sketcher::SketchObject] Sketch019
  FullyConstrained = true
  sketch-geometry (7):
    g0: LineSegment StartX=0 StartY=0 StartZ=0 EndX=0 EndY=6 EndZ=0
    g1: Circle CenterX=0 CenterY=0 CenterZ=0 NormalX=0 NormalY=0 NormalZ=1 AngleXU=0 Radius=1
    g2: Circle CenterX=8 CenterY=6 CenterZ=0 NormalX=0 NormalY=0 NormalZ=1 AngleXU=0 Radius=1
    g3: BSplineCurve PolesCount=3 KnotsCount=2 Degree=2 IsPeriodic=0
    g4: GeomPoint X=0 Y=0 Z=0
    g5: GeomPoint X=8 Y=6 Z=0
    g6: LineSegment StartX=0 StartY=6 StartZ=0 EndX=8 EndY=6 EndZ=0
  constraints (14):
    c: Coincident(g0,g-1)
    c: Distance(g0) = 6
    c: Vertical(g0)
    c: Coincident(g3,g0)
    c: Weight(g1) = 1
    c: Equal(g1,g2)
    c: InternalAlignment(g1,g3)
    c: InternalAlignment(g2,g3)
    c: InternalAlignment(g4,g3)
    c: InternalAlignment(g5,g3)
    c: Block(g3)
    c: Coincident(g6,g0)
    c: Coincident(g6,g3)
    c: Horizontal(g6)
FEATURE [Part::Extrusion] Extrude013  label="caseScrewPillarBracket001"
  Base = -> Sketch019
  Dir = (0,0,1)
  DirMode = 2
  FaceMakerClass = Part::FaceMakerBullseye
  LengthFwd = 2.4
  LengthRev = 0
  Placement = pos=(15.76,29,60.8) rot=(0,0,1;0rad)
  Solid = true
  Symmetric = false
FEATURE [Sketcher::SketchObject] Sketch020
  FullyConstrained = true
  sketch-geometry (7):
    g0: LineSegment StartX=0 StartY=0 StartZ=0 EndX=0 EndY=6 EndZ=0
    g1: Circle CenterX=0 CenterY=0 CenterZ=0 NormalX=0 NormalY=0 NormalZ=1 AngleXU=0 Radius=1
    g2: Circle CenterX=8 CenterY=6 CenterZ=0 NormalX=0 NormalY=0 NormalZ=1 AngleXU=0 Radius=1
    g3: BSplineCurve PolesCount=3 KnotsCount=2 Degree=2 IsPeriodic=0
    g4: GeomPoint X=0 Y=0 Z=0
    g5: GeomPoint X=8 Y=6 Z=0
    g6: LineSegment StartX=0 StartY=6 StartZ=0 EndX=8 EndY=6 EndZ=0
  constraints (14):
    c: Coincident(g0,g-1)
    c: Distance(g0) = 6
    c: Vertical(g0)
    c: Coincident(g3,g0)
    c: Weight(g1) = 1
    c: Equal(g1,g2)
    c: InternalAlignment(g1,g3)
    c: InternalAlignment(g2,g3)
    c: InternalAlignment(g4,g3)
    c: InternalAlignment(g5,g3)
    c: Block(g3)
    c: Coincident(g6,g0)
    c: Coincident(g6,g3)
    c: Horizontal(g6)
FEATURE [Part::Extrusion] Extrude014  label="caseScrewPillarBracket002"
  Base = -> Sketch020
  Dir = (0,0,1)
  DirMode = 2
  FaceMakerClass = Part::FaceMakerBullseye
  LengthFwd = 2.4
  LengthRev = 0
  Placement = pos=(13.7,29,13.26) rot=(0,1,0;-1.5708rad)
  Solid = true
  Symmetric = false
FEATURE [Sketcher::SketchObject] Sketch021
  FullyConstrained = true
  sketch-geometry (7):
    g0: LineSegment StartX=0 StartY=0 StartZ=0 EndX=0 EndY=6 EndZ=0
    g1: Circle CenterX=0 CenterY=0 CenterZ=0 NormalX=0 NormalY=0 NormalZ=1 AngleXU=0 Radius=1
    g2: Circle CenterX=8 CenterY=6 CenterZ=0 NormalX=0 NormalY=0 NormalZ=1 AngleXU=0 Radius=1
    g3: BSplineCurve PolesCount=3 KnotsCount=2 Degree=2 IsPeriodic=0
    g4: GeomPoint X=0 Y=0 Z=0
    g5: GeomPoint X=8 Y=6 Z=0
    g6: LineSegment StartX=0 StartY=6 StartZ=0 EndX=8 EndY=6 EndZ=0
  constraints (14):
    c: Coincident(g0,g-1)
    c: Distance(g0) = 6
    c: Vertical(g0)
    c: Coincident(g3,g0)
    c: Weight(g1) = 1
    c: Equal(g1,g2)
    c: InternalAlignment(g1,g3)
    c: InternalAlignment(g2,g3)
    c: InternalAlignment(g4,g3)
    c: InternalAlignment(g5,g3)
    c: Block(g3)
    c: Coincident(g6,g0)
    c: Coincident(g6,g3)
    c: Horizontal(g6)
FEATURE [Part::Extrusion] Extrude015  label="caseScrewPillarBracket003"
  Base = -> Sketch021
  Dir = (0,0,1)
  DirMode = 2
  FaceMakerClass = Part::FaceMakerBullseye
  LengthFwd = 2.4
  LengthRev = 0
  Placement = pos=(11.3,29,58.74) rot=(0,1,0;1.5708rad)
  Solid = true
  Symmetric = false
FEATURE [Sketcher::SketchObject] Sketch022
  FullyConstrained = true
  sketch-geometry (7):
    g0: LineSegment StartX=0 StartY=0 StartZ=0 EndX=0 EndY=6 EndZ=0
    g1: Circle CenterX=0 CenterY=0 CenterZ=0 NormalX=0 NormalY=0 NormalZ=1 AngleXU=0 Radius=1
    g2: Circle CenterX=8 CenterY=6 CenterZ=0 NormalX=0 NormalY=0 NormalZ=1 AngleXU=0 Radius=1
    g3: BSplineCurve PolesCount=3 KnotsCount=2 Degree=2 IsPeriodic=0
    g4: GeomPoint X=0 Y=0 Z=0
    g5: GeomPoint X=8 Y=6 Z=0
    g6: LineSegment StartX=0 StartY=6 StartZ=0 EndX=8 EndY=6 EndZ=0
  constraints (14):
    c: Coincident(g0,g-1)
    c: Distance(g0) = 6
    c: Vertical(g0)
    c: Coincident(g3,g0)
    c: Weight(g1) = 1
    c: Equal(g1,g2)
    c: InternalAlignment(g1,g3)
    c: InternalAlignment(g2,g3)
    c: InternalAlignment(g4,g3)
    c: InternalAlignment(g5,g3)
    c: Block(g3)
    c: Coincident(g6,g0)
    c: Coincident(g6,g3)
    c: Horizontal(g6)
FEATURE [Part::Extrusion] Extrude016  label="caseScrewPillarBracket004"
  Base = -> Sketch022
  Dir = (0,0,1)
  DirMode = 2
  FaceMakerClass = Part::FaceMakerBullseye
  LengthFwd = 2.4
  LengthRev = 0
  Placement = pos=(88.3,29,65.23) rot=(0,1,0;1.5708rad)
  Solid = true
  Symmetric = false
FEATURE [Sketcher::SketchObject] Sketch023
  FullyConstrained = true
  sketch-geometry (7):
    g0: LineSegment StartX=0 StartY=0 StartZ=0 EndX=0 EndY=6 EndZ=0
    g1: Circle CenterX=0 CenterY=0 CenterZ=0 NormalX=0 NormalY=0 NormalZ=1 AngleXU=0 Radius=1
    g2: Circle CenterX=8 CenterY=6 CenterZ=0 NormalX=0 NormalY=0 NormalZ=1 AngleXU=0 Radius=1
    g3: BSplineCurve PolesCount=3 KnotsCount=2 Degree=2 IsPeriodic=0
    g4: GeomPoint X=0 Y=0 Z=0
    g5: GeomPoint X=8 Y=6 Z=0
    g6: LineSegment StartX=0 StartY=6 StartZ=0 EndX=8 EndY=6 EndZ=0
  constraints (14):
    c: Coincident(g0,g-1)
    c: Distance(g0) = 6
    c: Vertical(g0)
    c: Coincident(g3,g0)
    c: Weight(g1) = 1
    c: Equal(g1,g2)
    c: InternalAlignment(g1,g3)
    c: InternalAlignment(g2,g3)
    c: InternalAlignment(g4,g3)
    c: InternalAlignment(g5,g3)
    c: Block(g3)
    c: Coincident(g6,g0)
    c: Coincident(g6,g3)
    c: Horizontal(g6)
FEATURE [Part::Extrusion] Extrude017  label="caseScrewPillarBracket005"
  Base = -> Sketch023
  Dir = (0,0,1)
  DirMode = 2
  FaceMakerClass = Part::FaceMakerBullseye
  LengthFwd = 2.4
  LengthRev = 0
  Placement = pos=(90.7,29,6.77) rot=(0,-1,0;1.5708rad)
  Solid = true
  Symmetric = false
FEATURE [Sketcher::SketchObject] Sketch024
  FullyConstrained = true
  sketch-geometry (7):
    g0: LineSegment StartX=0 StartY=0 StartZ=0 EndX=0 EndY=6 EndZ=0
    g1: Circle CenterX=0 CenterY=0 CenterZ=0 NormalX=0 NormalY=0 NormalZ=1 AngleXU=0 Radius=1
    g2: Circle CenterX=8 CenterY=6 CenterZ=0 NormalX=0 NormalY=0 NormalZ=1 AngleXU=0 Radius=1
    g3: BSplineCurve PolesCount=3 KnotsCount=2 Degree=2 IsPeriodic=0
    g4: GeomPoint X=0 Y=0 Z=0
    g5: GeomPoint X=8 Y=6 Z=0
    g6: LineSegment StartX=0 StartY=6 StartZ=0 EndX=8 EndY=6 EndZ=0
  constraints (14):
    c: Coincident(g0,g-1)
    c: Distance(g0) = 6
    c: Vertical(g0)
    c: Coincident(g3,g0)
    c: Weight(g1) = 1
    c: Equal(g1,g2)
    c: InternalAlignment(g1,g3)
    c: InternalAlignment(g2,g3)
    c: InternalAlignment(g4,g3)
    c: InternalAlignment(g5,g3)
    c: Block(g3)
    c: Coincident(g6,g0)
    c: Coincident(g6,g3)
    c: Horizontal(g6)
FEATURE [Part::Extrusion] Extrude018  label="caseScrewPillarBracket006"
  Base = -> Sketch024
  Dir = (0,0,1)
  DirMode = 2
  FaceMakerClass = Part::FaceMakerBullseye
  LengthFwd = 2.4
  LengthRev = 0
  Placement = pos=(103.7,29,6.77) rot=(0,-1,0;1.5708rad)
  Solid = true
  Symmetric = false
FEATURE [Sketcher::SketchObject] Sketch025
  FullyConstrained = true
  sketch-geometry (7):
    g0: LineSegment StartX=0 StartY=0 StartZ=0 EndX=0 EndY=6 EndZ=0
    g1: Circle CenterX=0 CenterY=0 CenterZ=0 NormalX=0 NormalY=0 NormalZ=1 AngleXU=0 Radius=1
    g2: Circle CenterX=8 CenterY=6 CenterZ=0 NormalX=0 NormalY=0 NormalZ=1 AngleXU=0 Radius=1
    g3: BSplineCurve PolesCount=3 KnotsCount=2 Degree=2 IsPeriodic=0
    g4: GeomPoint X=0 Y=0 Z=0
    g5: GeomPoint X=8 Y=6 Z=0
    g6: LineSegment StartX=0 StartY=6 StartZ=0 EndX=8 EndY=6 EndZ=0
  constraints (14):
    c: Coincident(g0,g-1)
    c: Distance(g0) = 6
    c: Vertical(g0)
    c: Coincident(g3,g0)
    c: Weight(g1) = 1
    c: Equal(g1,g2)
    c: InternalAlignment(g1,g3)
    c: InternalAlignment(g2,g3)
    c: InternalAlignment(g4,g3)
    c: InternalAlignment(g5,g3)
    c: Block(g3)
    c: Coincident(g6,g0)
    c: Coincident(g6,g3)
    c: Horizontal(g6)
FEATURE [Part::Extrusion] Extrude019  label="caseScrewPillarBracket007"
  Base = -> Sketch025
  Dir = (0,0,1)
  DirMode = 2
  FaceMakerClass = Part::FaceMakerBullseye
  LengthFwd = 2.4
  LengthRev = 0
  Placement = pos=(101.3,29,65.23) rot=(0,1,0;1.5708rad)
  Solid = true
  Symmetric = false
FEATURE [Part::Box] Box011  label="frontCaseScrewPillarBracket"
  AttacherType = Attacher::AttachEngine3D
  Height = 2.4
  Length = 16
  Placement = pos=(87,28,2.3) rot=(0,0,1;0rad)
  Width = 7
FEATURE [Part::Box] Box012  label="frontCaseScrewPillarBracket001"
  AttacherType = Attacher::AttachEngine3D
  Height = 2.4
  Length = 16
  Placement = pos=(87,28,67.3) rot=(0,0,1;0rad)
  Width = 7
FEATURE [Sketcher::SketchObject] Sketch026
  FullyConstrained = true
  sketch-geometry (17):
    g0: Circle CenterX=-3.5 CenterY=23.5 CenterZ=0 NormalX=0 NormalY=0 NormalZ=1 AngleXU=0 Radius=1
    g1: Circle CenterX=-1 CenterY=15.25 CenterZ=0 NormalX=0 NormalY=0 NormalZ=1 AngleXU=0 Radius=1
    g2: Circle CenterX=-3.5 CenterY=7 CenterZ=0 NormalX=0 NormalY=0 NormalZ=1 AngleXU=0 Radius=1
    g3: BSplineCurve PolesCount=3 KnotsCount=2 Degree=2 IsPeriodic=0
    g4: GeomPoint X=-3.5 Y=23.5 Z=0
    g5: GeomPoint X=-3.5 Y=7 Z=0
    g6: Circle CenterX=-4.8 CenterY=30.5 CenterZ=0 NormalX=0 NormalY=0 NormalZ=1 AngleXU=0 Radius=1
    g7: Circle CenterX=-3.5 CenterY=30.5 CenterZ=0 NormalX=0 NormalY=0 NormalZ=1 AngleXU=0 Radius=1
    g8: Circle CenterX=-3.5 CenterY=29.2 CenterZ=0 NormalX=0 NormalY=0 NormalZ=1 AngleXU=0 Radius=1
    g9: BSplineCurve PolesCount=3 KnotsCount=2 Degree=2 IsPeriodic=0
    g10: GeomPoint X=-4.8 Y=30.5 Z=0
    g11: GeomPoint X=-3.5 Y=29.2 Z=0
    g12: LineSegment StartX=-3.5 StartY=29.2 StartZ=0 EndX=-3.5 EndY=23.5 EndZ=0
    g13: LineSegment StartX=-4.8 StartY=30.5 StartZ=0 EndX=0 EndY=30.5 EndZ=0
    g14: LineSegment StartX=-3.5 StartY=5 StartZ=0 EndX=-3.5 EndY=7 EndZ=0
    g15: LineSegment StartX=0 StartY=5 StartZ=0 EndX=0 EndY=30.5 EndZ=0
    g16: LineSegment StartX=-3.5 StartY=5 StartZ=0 EndX=0 EndY=5 EndZ=0
  constraints (33):
    c: Weight(g0) = 1
    c: Equal(g0,g1)
    c: Equal(g0,g2)
    c: InternalAlignment(g0,g3)
    c: InternalAlignment(g1,g3)
    c: InternalAlignment(g2,g3)
    c: InternalAlignment(g4,g3)
    c: InternalAlignment(g5,g3)
    c: Block(g3)
    c: Weight(g6) = 1
    c: Equal(g6,g7)
    c: Equal(g6,g8)
    c: InternalAlignment(g6,g9)
    c: InternalAlignment(g7,g9)
    c: InternalAlignment(g8,g9)
    c: InternalAlignment(g10,g9)
    c: InternalAlignment(g11,g9)
    c: Block(g9)
    c: Coincident(g12,g9)
    c: Coincident(g12,g3)
    c: Vertical(g12)
    c: Coincident(g13,g9)
    c: Horizontal(g13)
    c: Distance(g13) = 4.8
    c: Coincident(g14,g3)
    c: Vertical(g14)
    c: Coincident(g15,g13)
    c: Vertical(g15)
    c: Tangent(g15,g1)
    c: Distance(g14) = 2
    c: Coincident(g16,g14)
    c: Horizontal(g16)
    c: Coincident(g15,g16)
FEATURE [Part::Feature] Face050
  shape: bbox 4.8 x 25.5 x 2e-07 mm, 1 faces, 0 solids (baked)
FEATURE [Part::Revolution] Revolve054  label="moreFrontCaseScrewPost001"
  Angle = 360
  Axis = (0,1,0)
  Base = (0,0,0)
  FaceMakerClass = Part::FaceMakerBullseye
  Placement = pos=(102.5,4.5,3.5) rot=(0,0,1;0rad)
  Solid = false
  Source = -> Face050
  Symmetric = false
FEATURE [Part::Feature] Face051
  shape: bbox 4.8 x 25.5 x 2e-07 mm, 1 faces, 0 solids (baked)
FEATURE [Part::Revolution] Revolve055  label="moreFrontCaseScrewPost002"
  Angle = 360
  Axis = (0,1,0)
  Base = (0,0,0)
  FaceMakerClass = Part::FaceMakerBullseye
  Placement = pos=(102.5,4.5,68.5) rot=(0,0,1;0rad)
  Solid = false
  Source = -> Face051
  Symmetric = false
FEATURE [Sketcher::SketchObject] Sketch027
  FullyConstrained = true
  sketch-geometry (10):
    g0: LineSegment StartX=-1.6 StartY=4.7 StartZ=0 EndX=-1.6 EndY=1.7 EndZ=0
    g1: LineSegment StartX=-3.5 StartY=4.7 StartZ=0 EndX=-1.6 EndY=4.7 EndZ=0
    g2: LineSegment StartX=-1.6 StartY=1.7 StartZ=0 EndX=-1.6 EndY=1.5 EndZ=0
    g3: LineSegment StartX=-1.6 StartY=1.5 StartZ=0 EndX=-5.2 EndY=1.5 EndZ=0
    g4: Circle CenterX=-3.5 CenterY=4.7 CenterZ=0 NormalX=0 NormalY=0 NormalZ=1 AngleXU=0 Radius=1
    g5: Circle CenterX=-3.59627 CenterY=2.99743 CenterZ=0 NormalX=0 NormalY=0 NormalZ=1 AngleXU=0 Radius=1
    g6: Circle CenterX=-5.2 CenterY=1.5 CenterZ=0 NormalX=0 NormalY=0 NormalZ=1 AngleXU=0 Radius=1
    g7: BSplineCurve PolesCount=3 KnotsCount=2 Degree=2 IsPeriodic=0
    g8: GeomPoint X=-3.5 Y=4.7 Z=0
    g9: GeomPoint X=-5.2 Y=1.5 Z=0
  constraints (23):
    c: Vertical(g0)
    c: Distance(g0) = 3
    c: Coincident(g1,g0)
    c: Horizontal(g1)
    c: Block(g0)
    c: Block(g1)
    c: Coincident(g2,g0)
    c: Vertical(g2)
    c: Distance(g2) = 0.2
    c: Coincident(g3,g2)
    c: Horizontal(g3)
    c: Block(g3)
    c: Coincident(g7,g1)
    c: Weight(g4) = 1
    c: Equal(g4,g5)
    c: Equal(g4,g6)
    c: Coincident(g7,g3)
    c: InternalAlignment(g4,g7)
    c: InternalAlignment(g5,g7)
    c: InternalAlignment(g6,g7)
    c: InternalAlignment(g8,g7)
    c: InternalAlignment(g9,g7)
    c: Block(g7)
FEATURE [Sketcher::SketchObject] Sketch028
  FullyConstrained = true
  sketch-geometry (18):
    g0: LineSegment StartX=0 StartY=3e-16 StartZ=0 EndX=0 EndY=1.7 EndZ=0
    g1: LineSegment StartX=-3.5 StartY=0 StartZ=0 EndX=-3.5 EndY=0.9 EndZ=0
    g2: Circle CenterX=-2.7 CenterY=1.7 CenterZ=0 NormalX=0 NormalY=0 NormalZ=1 AngleXU=0 Radius=1
    g3: Circle CenterX=-3.5 CenterY=1.7 CenterZ=0 NormalX=0 NormalY=0 NormalZ=1 AngleXU=0 Radius=1
    g4: Circle CenterX=-3.5 CenterY=0.9 CenterZ=0 NormalX=0 NormalY=0 NormalZ=1 AngleXU=0 Radius=1
    g5: BSplineCurve PolesCount=3 KnotsCount=2 Degree=2 IsPeriodic=0
    g6: GeomPoint X=-2.7 Y=1.7 Z=0
    g7: GeomPoint X=-3.5 Y=0.9 Z=0
    g8: LineSegment StartX=-3.5 StartY=0 StartZ=0 EndX=-3.5 EndY=-7 EndZ=0
    g9: LineSegment StartX=0 StartY=3e-16 StartZ=0 EndX=0 EndY=-7 EndZ=0
    g10: LineSegment StartX=-3.5 StartY=-7 StartZ=0 EndX=0 EndY=-7 EndZ=0
    g11: LineSegment StartX=-2.7 StartY=1.7 StartZ=0 EndX=-1.6 EndY=1.7 EndZ=0
    g12: LineSegment StartX=0 StartY=1.7 StartZ=0 EndX=0 EndY=4.5 EndZ=0
    g13: LineSegment StartX=0 StartY=4.5 StartZ=0 EndX=0 EndY=10.8 EndZ=0
    g14: LineSegment StartX=0 StartY=10.8 StartZ=0 EndX=-2 EndY=10.8 EndZ=0
    g15: LineSegment StartX=-1.6 StartY=4.7 StartZ=0 EndX=-1.6 EndY=1.7 EndZ=0
    g16: LineSegment StartX=-1.6 StartY=4.7 StartZ=0 EndX=-2 EndY=4.7 EndZ=0
    g17: LineSegment StartX=-2 StartY=4.7 StartZ=0 EndX=-2 EndY=10.8 EndZ=0
  constraints (44):
    c: Vertical(g0)
    c: Vertical(g1)
    c: Distance(g1) = 0.9
    c: Block(g0)
    c: Distance(g0) = 1.7
    c: Weight(g2) = 1
    c: Equal(g2,g3)
    c: Equal(g2,g4)
    c: Coincident(g5,g1)
    c: InternalAlignment(g2,g5)
    c: InternalAlignment(g3,g5)
    c: InternalAlignment(g4,g5)
    c: InternalAlignment(g6,g5)
    c: InternalAlignment(g7,g5)
    c: Block(g5)
    c: Coincident(g8,g1)
    c: Vertical(g8)
    c: Distance(g8) = 7
    c: Vertical(g9)
    c: Equal(g8,g9) = 7
    c: Coincident(g9,g0)
    c: Coincident(g10,g8)
    c: Coincident(g10,g9)
    c: Horizontal(g10)
    c: Coincident(g11,g5)
    c: Horizontal(g11)
    c: Coincident(g12,g0)
    c: Vertical(g12)
    c: Distance(g12) = 2.8
    c: Coincident(g13,g12)
    c: Vertical(g13)
    c: Distance(g13) = 6.3
    c: Coincident(g14,g13)
    c: Horizontal(g14)
    c: Distance(g14) = 2
    c: Vertical(g15)
    c: Distance(g15) = 3
    c: Block(g11)
    c: Coincident(g15,g11)
    c: Coincident(g16,g15)
    c: Horizontal(g16)
    c: Coincident(g17,g16)
    c: Coincident(g17,g14)
    c: Vertical(g17)
FEATURE [Part::Revolution] Revolve040  label="backCaseScrewRetainer001"
  Angle = 360
  Axis = (0,1,0)
  Base = (0,0,0)
  FaceMakerClass = Part::FaceMakerBullseye
  Placement = pos=(12.5,3,10) rot=(0,0,1;0rad)
  Solid = false
  Source = -> Face036
  Symmetric = false
FEATURE [Part::Feature] Face055
  shape: bbox 3.5 x 30.2 x 2e-07 mm, 1 faces, 0 solids (baked)
FEATURE [Part::Revolution] Revolve059  label="backCaseScrewPost"
  Angle = 360
  Axis = (0,1,0)
  Base = (0,0,0)
  FaceMakerClass = Part::FaceMakerBullseye
  Placement = pos=(12.5,4.5,10) rot=(0,0,1;0rad)
  Solid = false
  Source = -> Face055
  Symmetric = false
FEATURE [Part::Feature] Face056
  shape: bbox 3.5 x 30.2 x 2e-07 mm, 1 faces, 0 solids (baked)
FEATURE [Part::Revolution] Revolve060  label="backCaseScrewPost001"
  Angle = 360
  Axis = (0,1,0)
  Base = (0,0,0)
  FaceMakerClass = Part::FaceMakerBullseye
  Placement = pos=(12.5,4.5,62) rot=(0,0,1;0rad)
  Solid = false
  Source = -> Face056
  Symmetric = false
FEATURE [Part::Feature] Face057
  shape: bbox 3.5 x 17.8 x 2e-07 mm, 1 faces, 0 solids (baked)
FEATURE [Part::Revolution] Revolve061  label="removeToCreateScrewAndThreadedInsertHole"
  Angle = 360
  Axis = (0,1,0)
  Base = (0,0,0)
  FaceMakerClass = Part::FaceMakerBullseye
  Placement = pos=(12.5,0,10) rot=(0,0,1;0rad)
  Solid = false
  Source = -> Face057
  Symmetric = false
FEATURE [Part::Feature] Face058
  shape: bbox 3.5 x 17.8 x 2e-07 mm, 1 faces, 0 solids (baked)
FEATURE [Part::Revolution] Revolve062  label="removeToCreateScrewAndThreadedInsertHole001"
  Angle = 360
  Axis = (0,1,0)
  Base = (0,0,0)
  FaceMakerClass = Part::FaceMakerBullseye
  Placement = pos=(12.5,0,62) rot=(0,0,1;0rad)
  Solid = false
  Source = -> Face058
  Symmetric = false
FEATURE [Part::Feature] Face059
  shape: bbox 3.5 x 17.8 x 2e-07 mm, 1 faces, 0 solids (baked)
FEATURE [Part::Revolution] Revolve063  label="removeToCreateScrewAndThreadedInsertHole002"
  Angle = 360
  Axis = (0,1,0)
  Base = (0,0,0)
  FaceMakerClass = Part::FaceMakerBullseye
  Placement = pos=(89.5,0,68.5) rot=(0,0,1;0rad)
  Solid = false
  Source = -> Face059
  Symmetric = false
FEATURE [Part::Feature] Face060
  shape: bbox 3.5 x 17.8 x 2e-07 mm, 1 faces, 0 solids (baked)
FEATURE [Part::Revolution] Revolve064  label="removeToCreateScrewAndThreadedInsertHole003"
  Angle = 360
  Axis = (0,1,0)
  Base = (0,0,0)
  FaceMakerClass = Part::FaceMakerBullseye
  Placement = pos=(89.5,0,3.5) rot=(0,0,1;0rad)
  Solid = false
  Source = -> Face060
  Symmetric = false
FEATURE [Part::Feature] Face061
  shape: bbox 3.5 x 17.8 x 2e-07 mm, 1 faces, 0 solids (baked)
FEATURE [Part::Revolution] Revolve065  label="removeToCreateScrewAndThreadedInsertHole004"
  Angle = 360
  Axis = (0,1,0)
  Base = (0,0,0)
  FaceMakerClass = Part::FaceMakerBullseye
  Placement = pos=(102.5,4.7,3.5) rot=(0,0,1;0rad)
  Solid = false
  Source = -> Face061
  Symmetric = false
FEATURE [Part::Feature] Face062
  shape: bbox 3.5 x 17.8 x 2e-07 mm, 1 faces, 0 solids (baked)
FEATURE [Part::Revolution] Revolve066  label="removeToCreateScrewAndThreadedInsertHole005"
  Angle = 360
  Axis = (0,1,0)
  Base = (0,0,0)
  FaceMakerClass = Part::FaceMakerBullseye
  Placement = pos=(102.5,4.7,68.5) rot=(0,0,1;0rad)
  Solid = false
  Source = -> Face062
  Symmetric = false
FEATURE [Part::MultiFuse] Fusion047  label="makeHoles"
  Shapes = -> [Revolve066,Revolve065,Revolve064,Revolve063,Revolve062,Revolve061]
FEATURE [Part::Feature] Face063
  shape: bbox 3.6 x 3.2 x 2e-07 mm, 1 faces, 0 solids (baked)
FEATURE [Part::Revolution] Revolve067  label="moreFrontCaseScrewRetainer002"
  Angle = 360
  Axis = (0,1,0)
  Base = (0,0,0)
  FaceMakerClass = Part::FaceMakerBullseye
  Placement = pos=(102.5,4.5,68.5) rot=(0,0,1;0rad)
  Solid = false
  Source = -> Face063
  Symmetric = false
FEATURE [Part::Feature] Face064
  shape: bbox 3.6 x 3.2 x 2e-07 mm, 1 faces, 0 solids (baked)
FEATURE [Part::Revolution] Revolve068  label="moreFrontCaseScrewRetainer003"
  Angle = 360
  Axis = (0,1,0)
  Base = (0,0,0)
  FaceMakerClass = Part::FaceMakerBullseye
  Placement = pos=(102.5,4.5,3.5) rot=(0,0,1;0rad)
  Solid = false
  Source = -> Face064
  Symmetric = false
FEATURE [Part::Cut] Cut014  label="bottom003"
  Base = -> Cut007
  Tool = -> Fusion047
FEATURE [Part::Feature] Face065
  shape: bbox 3.5 x 17.8 x 2e-07 mm, 1 faces, 0 solids (baked)
FEATURE [Part::Revolution] Revolve069  label="removeToCreateScrewAndThreadedInsertHole006"
  Angle = 360
  Axis = (0,1,0)
  Base = (0,0,0)
  FaceMakerClass = Part::FaceMakerBullseye
  Placement = pos=(12.5,0,10) rot=(0,0,1;0rad)
  Solid = false
  Source = -> Face065
  Symmetric = false
FEATURE [Part::Feature] Face066
  shape: bbox 3.5 x 17.8 x 2e-07 mm, 1 faces, 0 solids (baked)
FEATURE [Part::Revolution] Revolve070  label="removeToCreateScrewAndThreadedInsertHole007"
  Angle = 360
  Axis = (0,1,0)
  Base = (0,0,0)
  FaceMakerClass = Part::FaceMakerBullseye
  Placement = pos=(12.5,0,62) rot=(0,0,1;0rad)
  Solid = false
  Source = -> Face066
  Symmetric = false
FEATURE [Part::Feature] Face067
  shape: bbox 3.5 x 17.8 x 2e-07 mm, 1 faces, 0 solids (baked)
FEATURE [Part::Revolution] Revolve071  label="removeToCreateScrewAndThreadedInsertHole008"
  Angle = 360
  Axis = (0,1,0)
  Base = (0,0,0)
  FaceMakerClass = Part::FaceMakerBullseye
  Placement = pos=(89.5,0,68.5) rot=(0,0,1;0rad)
  Solid = false
  Source = -> Face067
  Symmetric = false
FEATURE [Part::Feature] Face068
  shape: bbox 3.5 x 17.8 x 2e-07 mm, 1 faces, 0 solids (baked)
FEATURE [Part::Revolution] Revolve072  label="removeToCreateScrewAndThreadedInsertHole009"
  Angle = 360
  Axis = (0,1,0)
  Base = (0,0,0)
  FaceMakerClass = Part::FaceMakerBullseye
  Placement = pos=(89.5,0,3.5) rot=(0,0,1;0rad)
  Solid = false
  Source = -> Face068
  Symmetric = false
FEATURE [Part::Feature] Face069
  shape: bbox 3.5 x 17.8 x 2e-07 mm, 1 faces, 0 solids (baked)
FEATURE [Part::Feature] Face070
  shape: bbox 3.5 x 17.8 x 2e-07 mm, 1 faces, 0 solids (baked)
FEATURE [Part::Revolution] Revolve073  label="removeToCreateScrewAndThreadedInsertHole010"
  Angle = 360
  Axis = (0,1,0)
  Base = (0,0,0)
  FaceMakerClass = Part::FaceMakerBullseye
  Placement = pos=(102.5,4.7,3.5) rot=(0,0,1;0rad)
  Solid = false
  Source = -> Face069
  Symmetric = false
FEATURE [Part::Revolution] Revolve074  label="removeToCreateScrewAndThreadedInsertHole011"
  Angle = 360
  Axis = (0,1,0)
  Base = (0,0,0)
  FaceMakerClass = Part::FaceMakerBullseye
  Placement = pos=(102.5,4.7,68.5) rot=(0,0,1;0rad)
  Solid = false
  Source = -> Face070
  Symmetric = false
FEATURE [Part::MultiFuse] Fusion048  label="makeHoles001"
  Shapes = -> [Revolve074,Revolve073,Revolve072,Revolve071,Revolve070,Revolve069]
FEATURE [Part::MultiFuse] Fusion049  label="caseScrewRetainers"
  Shapes = -> [Revolve067,Revolve068,Revolve048,Revolve047,Revolve039,Revolve040]
FEATURE [Part::Cut] Cut015  label="caseScrewRetainers001"
  Base = -> Fusion049
  Tool = -> Fusion048
FEATURE [Part::MultiFuse] Fusion050  label="casePillars"
  Shapes = -> [Revolve055,Revolve054,Revolve043,Revolve046,Revolve059,Revolve060]
FEATURE [Part::Feature] Face071 .. Face076  x6 (patterned run collapsed; names and placements below)
  shape: bbox 3.5 x 17.8 x 2e-07 mm, 1 faces, 0 solids (baked)
FEATURE [Part::Revolution] Revolve075  label="removeToCreateScrewAndThreadedInsertHole012"
  Angle = 360
  Axis = (0,1,0)
  Base = (0,0,0)
  FaceMakerClass = Part::FaceMakerBullseye
  Placement = pos=(12.5,0,10) rot=(0,0,1;0rad)
  Solid = false
  Source = -> Face071
  Symmetric = false
FEATURE [Part::Revolution] Revolve076  label="removeToCreateScrewAndThreadedInsertHole013"
  Angle = 360
  Axis = (0,1,0)
  Base = (0,0,0)
  FaceMakerClass = Part::FaceMakerBullseye
  Placement = pos=(12.5,0,62) rot=(0,0,1;0rad)
  Solid = false
  Source = -> Face072
  Symmetric = false
FEATURE [Part::Revolution] Revolve077  label="removeToCreateScrewAndThreadedInsertHole014"
  Angle = 360
  Axis = (0,1,0)
  Base = (0,0,0)
  FaceMakerClass = Part::FaceMakerBullseye
  Placement = pos=(89.5,0,68.5) rot=(0,0,1;0rad)
  Solid = false
  Source = -> Face073
  Symmetric = false
FEATURE [Part::Revolution] Revolve078  label="removeToCreateScrewAndThreadedInsertHole015"
  Angle = 360
  Axis = (0,1,0)
  Base = (0,0,0)
  FaceMakerClass = Part::FaceMakerBullseye
  Placement = pos=(89.5,0,3.5) rot=(0,0,1;0rad)
  Solid = false
  Source = -> Face074
  Symmetric = false
FEATURE [Part::Revolution] Revolve079  label="removeToCreateScrewAndThreadedInsertHole016"
  Angle = 360
  Axis = (0,1,0)
  Base = (0,0,0)
  FaceMakerClass = Part::FaceMakerBullseye
  Placement = pos=(102.5,4.7,3.5) rot=(0,0,1;0rad)
  Solid = false
  Source = -> Face075
  Symmetric = false
FEATURE [Part::Revolution] Revolve080  label="removeToCreateScrewAndThreadedInsertHole017"
  Angle = 360
  Axis = (0,1,0)
  Base = (0,0,0)
  FaceMakerClass = Part::FaceMakerBullseye
  Placement = pos=(102.5,4.7,68.5) rot=(0,0,1;0rad)
  Solid = false
  Source = -> Face076
  Symmetric = false
FEATURE [Part::MultiFuse] Fusion051  label="makeHoles002"
  Shapes = -> [Revolve080,Revolve079,Revolve078,Revolve077,Revolve076,Revolve075]
FEATURE [Part::Cut] Cut016  label="caesPillars"
  Base = -> Fusion050
  Tool = -> Fusion051
FEATURE [Part::Revolution] Revolve009  label="plugHousing016"
  Angle = 360
  Axis = (0,1,0)
  Base = (0,0,0)
  FaceMakerClass = Part::FaceMakerBullseye
  Placement = pos=(0,0,36.15) rot=(0,0,1;0rad)
  Solid = false
  Source = -> Face012
  Symmetric = false
FEATURE [Part::MultiFuse] Fusion014  label="plugHousing023"
  Placement = pos=(0,0,0) rot=(0,0,1;1.5708rad)
  Shapes = -> [Revolve011,Revolve009]
FEATURE [Part::Revolution] Revolve010  label="plugHousing017"
  Angle = 360
  Axis = (0,1,0)
  Base = (0,0,0)
  FaceMakerClass = Part::FaceMakerBullseye
  Placement = pos=(0,0,36.15) rot=(0,0,1;0rad)
  Solid = false
  Source = -> Face014
  Symmetric = false
FEATURE [Part::MultiFuse] Fusion015  label="plugHousing024"
  Placement = pos=(0,0,0) rot=(0,0,1;1.5708rad)
  Shapes = -> [Revolve010,Revolve015]
FEATURE [Part::Revolution] Revolve014  label="plugHousing026"
  Angle = 360
  Axis = (0,1,0)
  Base = (0,0,0)
  FaceMakerClass = Part::FaceMakerBullseye
  Placement = pos=(0,0,36.15) rot=(0,0,1;0rad)
  Solid = false
  Source = -> Face011
  Symmetric = false
FEATURE [Part::Revolution] Revolve013  label="plugHousing025"
  Angle = 360
  Axis = (0,1,0)
  Base = (0,0,0)
  FaceMakerClass = Part::FaceMakerBullseye
  Placement = pos=(0,0,36.15) rot=(0,0,1;0rad)
  Solid = false
  Source = -> Face015
  Symmetric = false
FEATURE [Part::MultiFuse] Fusion016  label="plugHousing028"
  Placement = pos=(0,19,0) rot=(0,0,1;3.14159rad)
  Shapes = -> [Fusion014,Fusion013]
FEATURE [Part::MultiFuse] Fusion011  label="plugHousing018"
  Placement = pos=(0,0,0) rot=(0,0,1;1.5708rad)
  Shapes = -> [Revolve014,Revolve013]
FEATURE [Part::MultiFuse] Fusion012  label="plugHousing019"
  Placement = pos=(0,19,0) rot=(0,0,1;3.14159rad)
  Shapes = -> [Fusion011,Fusion015]
FEATURE [Part::MultiFuse] Fusion017  label="plugHousing029"
  Placement = pos=(122.621,0,-0.15) rot=(0,0,1;0rad)
  Shapes = -> [Fusion016,Fusion012]
FEATURE [Part::MultiFuse] Fusion052  label="casePillarRetainers"
  Shapes = -> [Extrude012,Extrude013,Extrude014,Extrude015,Extrude016,Extrude017,Extrude018,Extrude019,Box011,Box012]
FEATURE [Part::Feature] Face077
  shape: bbox 3.5 x 17.8 x 2e-07 mm, 1 faces, 0 solids (baked)
FEATURE [Part::Revolution] Revolve081  label="removeToCreateScrewAndThreadedInsertHole018"
  Angle = 360
  Axis = (0,1,0)
  Base = (0,0,0)
  FaceMakerClass = Part::FaceMakerBullseye
  Placement = pos=(62.3,30.3,19.7) rot=(0,0,1;0rad)
  Solid = false
  Source = -> Face077
  Symmetric = false
FEATURE [Part::Feature] Face078
  shape: bbox 3.5 x 17.8 x 2e-07 mm, 1 faces, 0 solids (baked)
FEATURE [Part::Revolution] Revolve082  label="removeToCreateScrewAndThreadedInsertHole019"
  Angle = 360
  Axis = (0,1,0)
  Base = (0,0,0)
  FaceMakerClass = Part::FaceMakerBullseye
  Placement = pos=(62.3,30.3,51.7) rot=(0,0,1;0rad)
  Solid = false
  Source = -> Face078
  Symmetric = false
FEATURE [Part::Feature] Face079
  shape: bbox 3.5 x 17.8 x 2e-07 mm, 1 faces, 0 solids (baked)
FEATURE [Part::Revolution] Revolve083  label="removeToCreateScrewAndThreadedInsertHole020"
  Angle = 360
  Axis = (0,1,0)
  Base = (0,0,0)
  FaceMakerClass = Part::FaceMakerBullseye
  Placement = pos=(30.3,30.3,19.7) rot=(0,0,1;0rad)
  Solid = false
  Source = -> Face079
  Symmetric = false
FEATURE [Part::Feature] Face080
  shape: bbox 3.5 x 17.8 x 2e-07 mm, 1 faces, 0 solids (baked)
FEATURE [Part::Revolution] Revolve084  label="removeToCreateScrewAndThreadedInsertHole021"
  Angle = 360
  Axis = (0,1,0)
  Base = (0,0,0)
  FaceMakerClass = Part::FaceMakerBullseye
  Placement = pos=(30.3,30.3,51.7) rot=(0,0,1;0rad)
  Solid = false
  Source = -> Face080
  Symmetric = false
FEATURE [Part::MultiFuse] Fusion053  label="createThreadedInsertHolesForFan"
  Shapes = -> [Revolve081,Revolve082,Revolve083,Revolve084]
FEATURE [Part::Cut] Cut017  label="fanScrewHousing001"
  Base = -> Fusion046
  Tool = -> Fusion053
FEATURE [Part::Feature] Face081
  shape: bbox 3.5 x 17.8 x 2e-07 mm, 1 faces, 0 solids (baked)
FEATURE [Part::Revolution] Revolve085  label="removeToCreateScrewAndThreadedInsertHole022"
  Angle = 360
  Axis = (0,1,0)
  Base = (0,0,0)
  FaceMakerClass = Part::FaceMakerBullseye
  Placement = pos=(62.3,30.3,19.7) rot=(0,0,1;0rad)
  Solid = false
  Source = -> Face081
  Symmetric = false
FEATURE [Part::Feature] Face082
  shape: bbox 3.5 x 17.8 x 2e-07 mm, 1 faces, 0 solids (baked)
FEATURE [Part::Revolution] Revolve086  label="removeToCreateScrewAndThreadedInsertHole023"
  Angle = 360
  Axis = (0,1,0)
  Base = (0,0,0)
  FaceMakerClass = Part::FaceMakerBullseye
  Placement = pos=(62.3,30.3,51.7) rot=(0,0,1;0rad)
  Solid = false
  Source = -> Face082
  Symmetric = false
FEATURE [Part::Feature] Face083
  shape: bbox 3.5 x 17.8 x 2e-07 mm, 1 faces, 0 solids (baked)
FEATURE [Part::Revolution] Revolve087  label="removeToCreateScrewAndThreadedInsertHole024"
  Angle = 360
  Axis = (0,1,0)
  Base = (0,0,0)
  FaceMakerClass = Part::FaceMakerBullseye
  Placement = pos=(30.3,30.3,19.7) rot=(0,0,1;0rad)
  Solid = false
  Source = -> Face083
  Symmetric = false
FEATURE [Part::Feature] Face084
  shape: bbox 3.5 x 17.8 x 2e-07 mm, 1 faces, 0 solids (baked)
FEATURE [Part::Revolution] Revolve088  label="removeToCreateScrewAndThreadedInsertHole025"
  Angle = 360
  Axis = (0,1,0)
  Base = (0,0,0)
  FaceMakerClass = Part::FaceMakerBullseye
  Placement = pos=(30.3,30.3,51.7) rot=(0,0,1;0rad)
  Solid = false
  Source = -> Face084
  Symmetric = false
FEATURE [Part::MultiFuse] Fusion054  label="createThreadedInsertHolesForFan001"
  Shapes = -> [Revolve085,Revolve086,Revolve087,Revolve088]
FEATURE [Part::Cut] Cut018  label="top007"
  Base = -> Fusion040
  Tool = -> Fusion054
FEATURE [Sketcher::SketchObject] Sketch029
  FullyConstrained = false
  Placement = pos=(0,0,0) rot=(1,0,0;1.5708rad)
  sketch-geometry (24):
    g0: ArcOfCircle CenterX=-4 CenterY=-10.5 CenterZ=0 NormalX=0 NormalY=0 NormalZ=1 AngleXU=0 Radius=1.5 StartAngle=6e-16 EndAngle=3.14159
    g1: ArcOfCircle CenterX=-34.2 CenterY=-10.5 CenterZ=0 NormalX=0 NormalY=0 NormalZ=1 AngleXU=0 Radius=1.5 StartAngle=0 EndAngle=3.14159
    g2: ArcOfCircle CenterX=-34.2 CenterY=-27.7 CenterZ=0 NormalX=0 NormalY=0 NormalZ=1 AngleXU=0 Radius=1.5 StartAngle=3.14159 EndAngle=6.28319
    g3: ArcOfCircle CenterX=-4 CenterY=-27.7 CenterZ=0 NormalX=0 NormalY=0 NormalZ=1 AngleXU=0 Radius=1.5 StartAngle=3.1416 EndAngle=6.28319
    g4: ArcOfCircle CenterX=-10 CenterY=-4.3 CenterZ=0 NormalX=0 NormalY=0 NormalZ=1 AngleXU=0 Radius=1.5 StartAngle=2e-16 EndAngle=3.14159
    g5: ArcOfCircle CenterX=-16.1 CenterY=-1.8 CenterZ=0 NormalX=0 NormalY=0 NormalZ=1 AngleXU=0 Radius=1.5 StartAngle=5e-16 EndAngle=3.14159
    g6: ArcOfCircle CenterX=-22.1 CenterY=-1.8 CenterZ=0 NormalX=0 NormalY=0 NormalZ=1 AngleXU=0 Radius=1.5 StartAngle=5e-16 EndAngle=3.14159
    g7: ArcOfCircle CenterX=-28.2 CenterY=-4.3 CenterZ=0 NormalX=0 NormalY=0 NormalZ=1 AngleXU=0 Radius=1.5 StartAngle=2e-16 EndAngle=3.14159
    g8: ArcOfCircle CenterX=-10 CenterY=-33.9 CenterZ=0 NormalX=0 NormalY=0 NormalZ=1 AngleXU=0 Radius=1.5 StartAngle=3.14159 EndAngle=6.28319
    g9: ArcOfCircle CenterX=-16.1 CenterY=-36.4 CenterZ=0 NormalX=0 NormalY=0 NormalZ=1 AngleXU=0 Radius=1.5 StartAngle=3.14159 EndAngle=6.28319
    g10: ArcOfCircle CenterX=-22.1 CenterY=-36.4 CenterZ=0 NormalX=0 NormalY=0 NormalZ=1 AngleXU=0 Radius=1.5 StartAngle=3.14159 EndAngle=6.28319
    g11: ArcOfCircle CenterX=-28.2 CenterY=-33.9 CenterZ=0 NormalX=0 NormalY=0 NormalZ=1 AngleXU=0 Radius=1.5 StartAngle=3.14159 EndAngle=6.28319
    g12: LineSegment StartX=-35.7 StartY=-10.5 StartZ=0 EndX=-35.7 EndY=-27.7 EndZ=0
    g13: LineSegment StartX=-32.7 StartY=-10.5 StartZ=0 EndX=-32.7 EndY=-27.7 EndZ=0
    g14: LineSegment StartX=-29.7 StartY=-33.9 StartZ=0 EndX=-29.7 EndY=-4.3 EndZ=0
    g15: LineSegment StartX=-26.7 StartY=-33.9 StartZ=0 EndX=-26.7 EndY=-4.3 EndZ=0
    g16: LineSegment StartX=-2.5 StartY=-10.5 StartZ=0 EndX=-2.5 EndY=-27.7 EndZ=0
    g17: LineSegment StartX=-8.5 StartY=-4.3 StartZ=0 EndX=-8.5 EndY=-33.9 EndZ=0
    g18: LineSegment StartX=-5.5 StartY=-10.5 StartZ=0 EndX=-5.5 EndY=-27.7 EndZ=0
    g19: LineSegment StartX=-11.5 StartY=-4.3 StartZ=0 EndX=-11.5 EndY=-33.9 EndZ=0
    g20: LineSegment StartX=-14.6 StartY=-1.8 StartZ=0 EndX=-14.6 EndY=-36.4 EndZ=0
    g21: LineSegment StartX=-17.6 StartY=-1.8 StartZ=0 EndX=-17.6 EndY=-36.4 EndZ=0
    g22: LineSegment StartX=-20.6 StartY=-36.4 StartZ=0 EndX=-20.6 EndY=-1.8 EndZ=0
    g23: LineSegment StartX=-23.6 StartY=-1.8 StartZ=0 EndX=-23.6 EndY=-36.4 EndZ=0
  constraints (48):
    c: Block(g0)
    c: Block(g1)
    c: Block(g2)
    c: Block(g3)
    c: Block(g4)
    c: Block(g5)
    c: Block(g6)
    c: Block(g7)
    c: Block(g8)
    c: Block(g9)
    c: Block(g10)
    c: Block(g11)
    c: Coincident(g12,g1)
    c: Coincident(g12,g2)
    c: Vertical(g12)
    c: Coincident(g13,g1)
    c: Coincident(g13,g2)
    c: Vertical(g13)
    c: Coincident(g14,g11)
    c: Coincident(g14,g7)
    c: Vertical(g14)
    c: Coincident(g15,g11)
    c: Coincident(g15,g7)
    c: Vertical(g15)
    c: Coincident(g16,g0)
    c: Coincident(g16,g3)
    c: Vertical(g16)
    c: Coincident(g17,g4)
    c: Coincident(g17,g8)
    c: Vertical(g17)
    c: Coincident(g18,g0)
    c: Coincident(g18,g3)
    c: Vertical(g18)
    c: Coincident(g19,g4)
    c: Coincident(g19,g8)
    c: Vertical(g19)
    c: Coincident(g20,g5)
    c: Coincident(g20,g9)
    c: Vertical(g20)
    c: Coincident(g21,g5)
    c: Coincident(g21,g9)
    c: Vertical(g21)
    c: Coincident(g22,g10)
    c: Coincident(g22,g6)
    c: Vertical(g22)
    c: Coincident(g23,g6)
    c: Coincident(g23,g10)
    c: Vertical(g23)
FEATURE [Part::Extrusion] Extrude020  label="removeToCreateFanGrillHoles"
  Base = -> Sketch029
  Dir = (0,-1,6e-16)
  DirMode = 2
  FaceMakerClass = Part::FaceMakerBullseye
  LengthFwd = 10
  LengthRev = 0
  Placement = pos=(65.4,44,54.82) rot=(0,0,1;0rad)
  Solid = true
  Symmetric = false
FEATURE [Part::MultiFuse] Fusion055  label="top008"
  Shapes = -> [Cut017,Cut018]
FEATURE [Part::Cut] Cut019  label="top009"
  Base = -> Fusion055
  Tool = -> Extrude020
FEATURE [App::MeasureDistance] Distance003  label="Distance: 71.95 mm"
  Distance = 71.9513
  P1 = (117,38,72)
  P2 = (117,38,0.0487319)
FEATURE [Sketcher::SketchObject] Sketch030
  FullyConstrained = false
  Placement = pos=(0,0,0) rot=(0.57735,0.57735,0.57735;2.0944rad)
  sketch-geometry (67):
    g0: LineSegment StartX=-3.1e-15 StartY=0 StartZ=0 EndX=-3.1e-15 EndY=19 EndZ=0
    g1: LineSegment StartX=0 StartY=53 StartZ=0 EndX=0 EndY=72 EndZ=0
    g2: ArcOfCircle CenterX=0 CenterY=36 CenterZ=0 NormalX=0 NormalY=0 NormalZ=1 AngleXU=0 Radius=17 StartAngle=1.5708 EndAngle=4.71239
    g3: LineSegment StartX=0 StartY=72 StartZ=0 EndX=-49.19 EndY=72 EndZ=0
    g4: LineSegment StartX=-3.1e-15 StartY=0 StartZ=0 EndX=-49.19 EndY=0 EndZ=0
    g5: LineSegment StartX=-49.19 StartY=69.25 StartZ=0 EndX=-49.19 EndY=66.25 EndZ=0
    g6: LineSegment StartX=-49.19 StartY=66.25 StartZ=0 EndX=-49.19 EndY=63.5 EndZ=0
    g7: LineSegment StartX=-49.19 StartY=63.5 StartZ=0 EndX=-49.19 EndY=60.5 EndZ=0
    g8: LineSegment StartX=-49.19 StartY=72 StartZ=0 EndX=-49.19 EndY=69.25 EndZ=0
    g9: LineSegment StartX=-49.19 StartY=57.75 StartZ=0 EndX=-49.19 EndY=54.75 EndZ=0
    g10: LineSegment StartX=-49.19 StartY=54.75 StartZ=0 EndX=-49.19 EndY=52 EndZ=0
    g11: LineSegment StartX=-49.19 StartY=52 StartZ=0 EndX=-49.19 EndY=49 EndZ=0
    g12: LineSegment StartX=-49.19 StartY=60.5 StartZ=0 EndX=-49.19 EndY=57.75 EndZ=0
    g13: LineSegment StartX=-49.19 StartY=46.25 StartZ=0 EndX=-49.19 EndY=43.25 EndZ=0
    g14: LineSegment StartX=-49.19 StartY=43.25 StartZ=0 EndX=-49.19 EndY=40.5 EndZ=0
    g15: LineSegment StartX=-49.19 StartY=40.5 StartZ=0 EndX=-49.19 EndY=37.5 EndZ=0
    g16: LineSegment StartX=-49.19 StartY=49 StartZ=0 EndX=-49.19 EndY=46.25 EndZ=0
    g17: LineSegment StartX=-49.19 StartY=34.5 StartZ=0 EndX=-49.19 EndY=31.5 EndZ=0
    g18: LineSegment StartX=-49.19 StartY=31.5 StartZ=0 EndX=-49.19 EndY=28.75 EndZ=0
    g19: LineSegment StartX=-49.19 StartY=28.75 StartZ=0 EndX=-49.19 EndY=25.75 EndZ=0
    g20: LineSegment StartX=-49.19 StartY=23 StartZ=0 EndX=-49.19 EndY=20 EndZ=0
    g21: LineSegment StartX=-49.19 StartY=20 StartZ=0 EndX=-49.19 EndY=17.25 EndZ=0
    g22: LineSegment StartX=-49.19 StartY=17.25 StartZ=0 EndX=-49.19 EndY=14.25 EndZ=0
    g23: LineSegment StartX=-49.19 StartY=25.75 StartZ=0 EndX=-49.19 EndY=23 EndZ=0
    g24: LineSegment StartX=-49.19 StartY=11.5 StartZ=0 EndX=-49.19 EndY=8.5 EndZ=0
    g25: LineSegment StartX=-49.19 StartY=8.5 StartZ=0 EndX=-49.19 EndY=5.75 EndZ=0
    g26: LineSegment StartX=-49.19 StartY=5.75 StartZ=0 EndX=-49.19 EndY=2.75 EndZ=0
    g27: LineSegment StartX=-49.19 StartY=14.25 StartZ=0 EndX=-49.19 EndY=11.5 EndZ=0
    g28: LineSegment StartX=-49.19 StartY=37.5 StartZ=0 EndX=-49.19 EndY=34.5 EndZ=0
    g29: LineSegment StartX=-49.19 StartY=2.75 StartZ=0 EndX=-49.19 EndY=0 EndZ=0
    g30: LineSegment StartX=-49.19 StartY=69.25 StartZ=0 EndX=0 EndY=69.25 EndZ=0
    g31: LineSegment StartX=0 StartY=69.25 StartZ=0 EndX=-1.5 EndY=69.25 EndZ=0
    g32: LineSegment StartX=-49.19 StartY=66.25 StartZ=0 EndX=7.66083e-07 EndY=66.25 EndZ=0
    g33: LineSegment StartX=-49.19 StartY=63.5 StartZ=0 EndX=7.66083e-07 EndY=63.5 EndZ=0
    g34: LineSegment StartX=-49.19 StartY=60.5 StartZ=0 EndX=7.66083e-07 EndY=60.5 EndZ=0
    g35: LineSegment StartX=-49.19 StartY=57.75 StartZ=0 EndX=7.66083e-07 EndY=57.75 EndZ=0
    g36: LineSegment StartX=-49.19 StartY=54.75 StartZ=0 EndX=7.66083e-07 EndY=54.75 EndZ=0
    g37: LineSegment StartX=-49.19 StartY=52 StartZ=0 EndX=-5.74456 EndY=52 EndZ=0
    g38: LineSegment StartX=-49.19 StartY=49 StartZ=0 EndX=-10.9545 EndY=49 EndZ=0
    g39: LineSegment StartX=-49.19 StartY=46.25 StartZ=0 EndX=-13.5624 EndY=46.25 EndZ=0
    g40: LineSegment StartX=-49.19 StartY=43.25 StartZ=0 EndX=-15.3765 EndY=43.25 EndZ=0
    g41: LineSegment StartX=-49.19 StartY=40.5 StartZ=0 EndX=-16.3936 EndY=40.5 EndZ=0
    g42: LineSegment StartX=-49.19 StartY=37.5 StartZ=0 EndX=-16.9337 EndY=37.5 EndZ=0
    g43: LineSegment StartX=-49.19 StartY=34.5 StartZ=0 EndX=-16.9337 EndY=34.5 EndZ=0
    g44: LineSegment StartX=-49.19 StartY=31.5 StartZ=0 EndX=-16.3936 EndY=31.5 EndZ=0
    g45: LineSegment StartX=-49.19 StartY=28.75 StartZ=0 EndX=-15.3765 EndY=28.75 EndZ=0
    g46: LineSegment StartX=-49.19 StartY=25.75 StartZ=0 EndX=-13.5624 EndY=25.75 EndZ=0
    g47: LineSegment StartX=-49.19 StartY=23 StartZ=0 EndX=-10.9545 EndY=23 EndZ=0
    g48: LineSegment StartX=-49.19 StartY=20 StartZ=0 EndX=-5.74456 EndY=20 EndZ=0
    g49: LineSegment StartX=-49.19 StartY=17.25 StartZ=0 EndX=7.66083e-07 EndY=17.25 EndZ=0
    g50: LineSegment StartX=-49.19 StartY=14.25 StartZ=0 EndX=7.66083e-07 EndY=14.25 EndZ=0
    g51: LineSegment StartX=-49.19 StartY=11.5 StartZ=0 EndX=7.66083e-07 EndY=11.5 EndZ=0
    g52: LineSegment StartX=-49.19 StartY=8.5 StartZ=0 EndX=7.66083e-07 EndY=8.5 EndZ=0
    g53: LineSegment StartX=-49.19 StartY=5.75 StartZ=0 EndX=7.66083e-07 EndY=5.75 EndZ=0
    g54: LineSegment StartX=-49.19 StartY=2.75 StartZ=0 EndX=7.66083e-07 EndY=2.75 EndZ=0
    g55: LineSegment StartX=7.66083e-07 StartY=66.25 StartZ=0 EndX=-1.5 EndY=66.25 EndZ=0
    g56: LineSegment StartX=7.66083e-07 StartY=63.5 StartZ=0 EndX=-1.5 EndY=63.5 EndZ=0
    g57: LineSegment StartX=7.66083e-07 StartY=60.5 StartZ=0 EndX=-1.5 EndY=60.5 EndZ=0
    g58: LineSegment StartX=7.66083e-07 StartY=57.75 StartZ=0 EndX=-1.5 EndY=57.75 EndZ=0
    g59: LineSegment StartX=7.66083e-07 StartY=54.75 StartZ=0 EndX=-1.5 EndY=54.75 EndZ=0
    g60: LineSegment StartX=7.66083e-07 StartY=17.25 StartZ=0 EndX=-1.5 EndY=17.25 EndZ=0
    g61: LineSegment StartX=7.66083e-07 StartY=14.25 StartZ=0 EndX=-1.5 EndY=14.25 EndZ=0
    g62: LineSegment StartX=7.66083e-07 StartY=11.5 StartZ=0 EndX=-1.5 EndY=11.5 EndZ=0
    g63: LineSegment StartX=7.66083e-07 StartY=8.5 StartZ=0 EndX=-1.5 EndY=8.5 EndZ=0
    g64: LineSegment StartX=7.66083e-07 StartY=5.75 StartZ=0 EndX=-1.5 EndY=5.75 EndZ=0
    g65: LineSegment StartX=7.66083e-07 StartY=2.75 StartZ=0 EndX=-1.5 EndY=2.75 EndZ=0
    g66: LineSegment StartX=7.9212 StartY=60.0463 StartZ=0 EndX=7.9212 EndY=61.5463 EndZ=0
  constraints (181):
    c: Coincident(g0,g-1)
    c: Distance(g0) = 19
    c: Vertical(g0)
    c: Equal(g0,g1) = 22
    c: Vertical(g1)
    c: Coincident(g2,g0)
    c: Block(g1)
    c: Block(g2)
    c: Coincident(g3,g1)
    c: Horizontal(g3)
    c: Distance(g3) = 49.19
    c: Coincident(g4,g0)
    c: Horizontal(g4)
    c: Block(g4)
    c: Vertical(g5)
    c: Distance(g5) = 3
    c: Block(g5)
    c: Coincident(g6,g5)
    c: Vertical(g6)
    c: Distance(g6) = 2.75
    c: Coincident(g7,g6)
    c: Vertical(g7)
    c: Distance(g7) = 3
    c: Coincident(g8,g3)
    c: Coincident(g8,g5)
    c: Vertical(g8)
    c: Distance(g8) = 2.75
    c: Vertical(g9)
    c: Equal(g5,g9) = 3
    c: Block(g9)
    c: Coincident(g10,g9)
    c: Vertical(g10)
    c: Equal(g6,g10) = 2.75
    c: Coincident(g11,g10)
    c: Vertical(g11)
    c: Equal(g7,g11) = 3
    c: Coincident(g12,g9)
    c: Vertical(g12)
    c: Equal(g8,g12) = 2.75
    c: Coincident(g12,g7)
    c: Vertical(g13)
    c: Equal(g5,g13) = 3
    c: Block(g13)
    c: Coincident(g14,g13)
    c: Vertical(g14)
    c: Equal(g6,g14) = 2.75
    c: Coincident(g15,g14)
    c: Vertical(g15)
    c: Equal(g7,g15) = 3
    c: Coincident(g16,g13)
    c: Vertical(g16)
    c: Equal(g8,g16) = 2.75
    c: Coincident(g16,g11)
    c: Vertical(g17)
    c: Equal(g5,g17) = 3
    c: Block(g17)
    c: Coincident(g18,g17)
    c: Vertical(g18)
    c: Equal(g6,g18) = 2.75
    c: Coincident(g19,g18)
    c: Vertical(g19)
    c: Equal(g7,g19) = 3
    c: Vertical(g20)
    c: Equal(g5,g20) = 3
    c: Block(g20)
    c: Coincident(g21,g20)
    c: Vertical(g21)
    c: Equal(g6,g21) = 2.75
    c: Coincident(g22,g21)
    c: Vertical(g22)
    c: Equal(g7,g22) = 3
    c: Coincident(g23,g20)
    c: Vertical(g23)
    c: Equal(g8,g23) = 2.75
    c: Coincident(g23,g19)
    c: Vertical(g24)
    c: Equal(g5,g24) = 3
    c: Block(g24)
    c: Coincident(g25,g24)
    c: Vertical(g25)
    c: Equal(g6,g25) = 2.75
    c: Coincident(g26,g25)
    c: Vertical(g26)
    c: Equal(g7,g26) = 3
    c: Coincident(g27,g24)
    c: Vertical(g27)
    c: Equal(g8,g27) = 2.75
    c: Coincident(g27,g22)
    c: Coincident(g28,g15)
    c: Coincident(g28,g17)
    c: Distance(g28) = 3
    c: Coincident(g29,g26)
    c: Coincident(g29,g4)
    c: Vertical(g29)
    c: Coincident(g30,g5)
    c: Horizontal(g30)
    c: PointOnObject(g30,g1)
    c: Horizontal(g31)
    c: Coincident(g31,g30)
    c: Horizontal(g32)
    c: Coincident(g32,g5)
    c: Horizontal(g33)
    c: Coincident(g33,g6)
    c: Horizontal(g34)
    c: Coincident(g34,g7)
    c: Horizontal(g35)
    c: Coincident(g35,g9)
    c: Horizontal(g36)
    c: Coincident(g36,g9)
    c: Horizontal(g37)
    c: Coincident(g37,g10)
    c: Horizontal(g38)
    c: Coincident(g38,g11)
    c: Horizontal(g39)
    c: Coincident(g39,g13)
    c: Horizontal(g40)
    c: Coincident(g40,g13)
    c: Horizontal(g41)
    c: Coincident(g41,g14)
    c: Horizontal(g42)
    c: Coincident(g42,g15)
    c: Horizontal(g43)
    c: Coincident(g43,g17)
    c: Horizontal(g44)
    c: Coincident(g44,g17)
    c: Horizontal(g45)
    c: Coincident(g45,g18)
    c: Horizontal(g46)
    c: Coincident(g46,g19)
    c: Horizontal(g47)
    c: Coincident(g47,g20)
    c: Horizontal(g48)
    c: Coincident(g48,g20)
    c: Horizontal(g49)
    c: Coincident(g49,g21)
    c: Horizontal(g50)
    c: Coincident(g50,g22)
    c: Horizontal(g51)
    c: Coincident(g51,g24)
    c: Horizontal(g52)
    c: Coincident(g52,g24)
    c: Horizontal(g53)
    c: Coincident(g53,g25)
    c: Horizontal(g54)
    c: Coincident(g54,g26)
    c: PointOnObject(g37,g2)
    c: PointOnObject(g38,g2)
    c: PointOnObject(g39,g2)
    c: PointOnObject(g40,g2)
    c: PointOnObject(g41,g2)
    c: PointOnObject(g42,g2)
    c: PointOnObject(g43,g2)
    c: PointOnObject(g44,g2)
    c: PointOnObject(g45,g2)
    c: PointOnObject(g46,g2)
    c: PointOnObject(g47,g2)
    c: PointOnObject(g48,g2)
    c: Horizontal(g55)
    c: Coincident(g55,g32)
    c: Horizontal(g56)
    c: Coincident(g56,g33)
    c: Horizontal(g57)
    c: Coincident(g57,g34)
    c: Horizontal(g58)
    c: Coincident(g58,g35)
    c: Horizontal(g59)
    c: Coincident(g59,g36)
    c: Horizontal(g60)
    c: Coincident(g60,g49)
    c: Horizontal(g61)
    c: Coincident(g61,g50)
    c: Horizontal(g62)
    c: Coincident(g62,g51)
    c: Horizontal(g63)
    c: Coincident(g63,g52)
    c: Horizontal(g64)
    c: Coincident(g64,g53)
    c: Horizontal(g65)
    c: Coincident(g65,g54)
    c: Vertical(g66)
    c: Distance(g66) = 1.5
